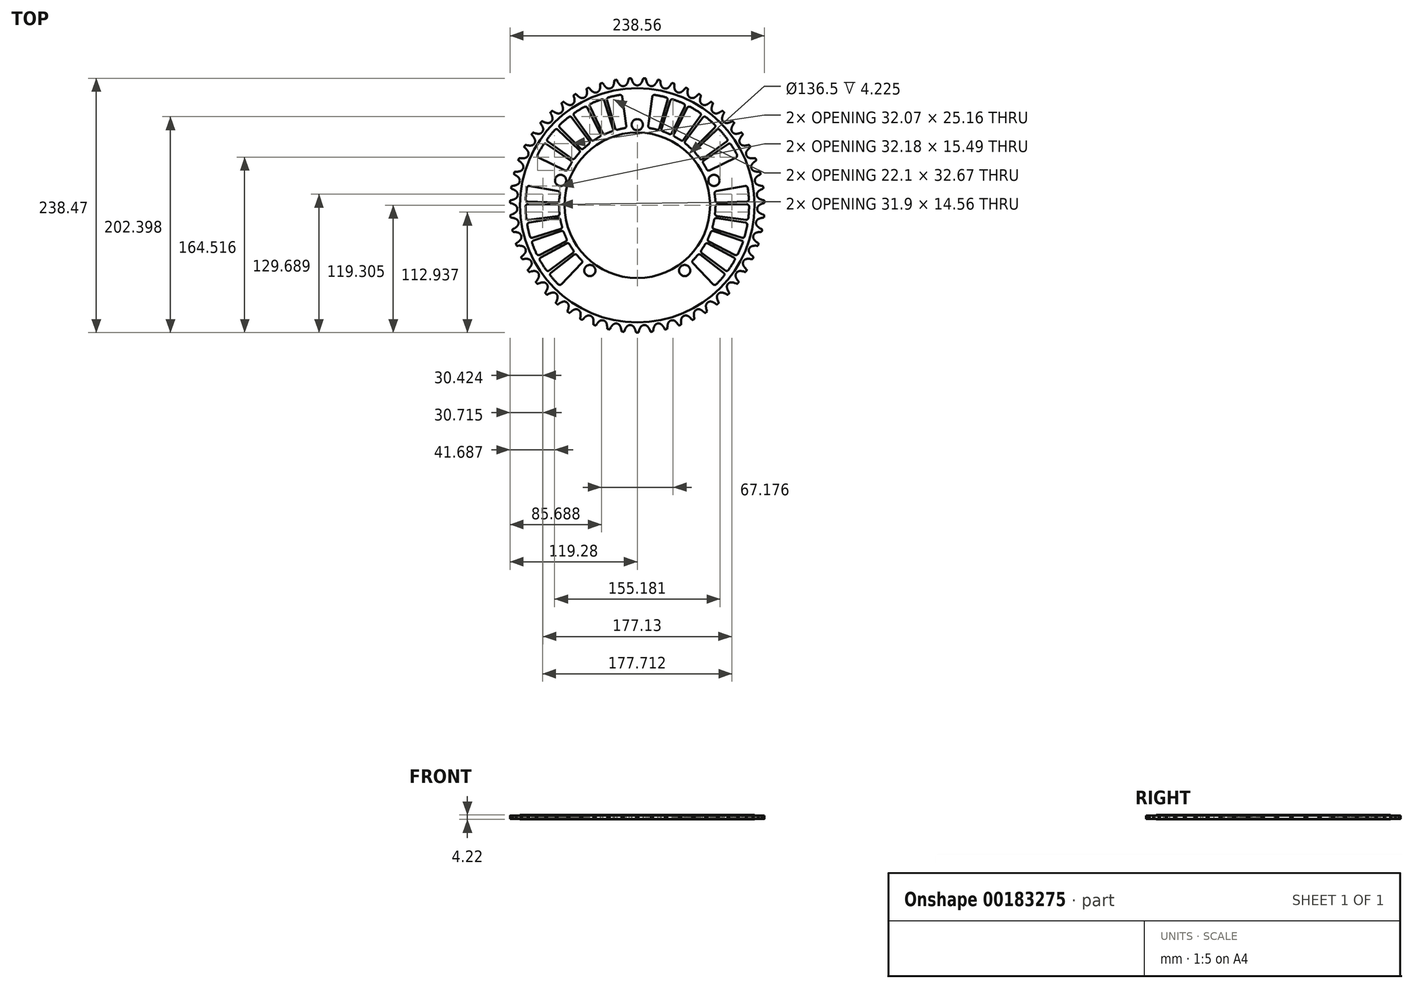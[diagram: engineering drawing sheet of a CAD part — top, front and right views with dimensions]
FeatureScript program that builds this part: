
annotation { "Feature Type Name" : "Feature", "Feature Type Description" : "" }
export const myFeature = defineFeature(function(context is Context, id is Id, definition is map)
    precondition{}
    {
        {
            var Q0;
            Q0=qCreatedBy(makeId("Top.planeOp"),FACE);
            var sketch = newSketch(context, id + "F0", { "sketchPlane" : qUnion([Q0])});
            skArc(sketch, "E0", {"start": v(-3.4, 114.25) * mm, "mid": v(-1.91, 112.97) * mm, "end": v(0, 112.52) * mm});
            skArc(sketch, "E1", {"start": v(-4.92, 117.1) * mm, "mid": v(-4.27, 115.62) * mm, "end": v(-3.4, 114.25) * mm});
            skLineSegment(sketch, "E2", {"start": v(-4.92, 117.1) * mm, "end": v(-5.32, 118.26) * mm});
            skArc(sketch, "E3", {"start": v(-5.32, 118.26) * mm, "mid": v(-5.97, 119.62) * mm, "end": v(-6.9, 120.8) * mm});
            skArc(sketch, "E4.MirrorCS", {"start": v(3.4, 114.25) * mm, "mid": v(1.91, 112.97) * mm, "end": v(0, 112.52) * mm});
            skArc(sketch, "E5.MirrorCS", {"start": v(4.92, 117.1) * mm, "mid": v(4.27, 115.62) * mm, "end": v(3.4, 114.25) * mm});
            skLineSegment(sketch, "E6.MirrorCS", {"start": v(4.92, 117.1) * mm, "end": v(5.32, 118.26) * mm});
            skArc(sketch, "E7.MirrorCS", {"start": v(5.32, 118.26) * mm, "mid": v(5.97, 119.62) * mm, "end": v(6.9, 120.8) * mm});
            skArc(sketch, "E8.1.0", {"start": v(-16.4, 113.12) * mm, "mid": v(-14.78, 112.02) * mm, "end": v(-12.83, 111.78) * mm});
            skArc(sketch, "E8.1.1", {"start": v(-8.2, 118.1) * mm, "mid": v(-7.7, 119.53) * mm, "end": v(-6.9, 120.8) * mm});
            skArc(sketch, "E8.1.2", {"start": v(-9.64, 113.9) * mm, "mid": v(-10.98, 112.46) * mm, "end": v(-12.83, 111.78) * mm});
            skArc(sketch, "E8.1.3", {"start": v(-8.46, 116.9) * mm, "mid": v(-8.94, 115.35) * mm, "end": v(-9.64, 113.9) * mm});
            skArc(sketch, "E8.1.4", {"start": v(-18.23, 115.77) * mm, "mid": v(-17.42, 114.38) * mm, "end": v(-16.4, 113.12) * mm});
            skArc(sketch, "E8.1.5", {"start": v(-18.77, 116.89) * mm, "mid": v(-19.57, 118.16) * mm, "end": v(-20.63, 119.23) * mm});
            skLineSegment(sketch, "E8.1.6", {"start": v(-18.23, 115.77) * mm, "end": v(-18.77, 116.89) * mm});
            skLineSegment(sketch, "E8.1.7", {"start": v(-8.46, 116.9) * mm, "end": v(-8.2, 118.1) * mm});
            skArc(sketch, "E8.2.0", {"start": v(-29.2, 110.5) * mm, "mid": v(-27.45, 109.6) * mm, "end": v(-25.48, 109.6) * mm});
            skArc(sketch, "E8.2.1", {"start": v(-21.6, 116.4) * mm, "mid": v(-21.28, 117.87) * mm, "end": v(-20.63, 119.23) * mm});
            skArc(sketch, "E8.2.2", {"start": v(-22.56, 112.05) * mm, "mid": v(-23.73, 110.47) * mm, "end": v(-25.48, 109.6) * mm});
            skArc(sketch, "E8.2.3", {"start": v(-21.73, 115.16) * mm, "mid": v(-22.03, 113.58) * mm, "end": v(-22.56, 112.05) * mm});
            skArc(sketch, "E8.2.4", {"start": v(-31.3, 112.94) * mm, "mid": v(-30.34, 111.65) * mm, "end": v(-29.2, 110.5) * mm});
            skArc(sketch, "E8.2.5", {"start": v(-31.97, 113.99) * mm, "mid": v(-32.9, 115.16) * mm, "end": v(-34.09, 116.1) * mm});
            skLineSegment(sketch, "E8.2.6", {"start": v(-31.3, 112.94) * mm, "end": v(-31.97, 113.99) * mm});
            skLineSegment(sketch, "E8.2.7", {"start": v(-21.73, 115.16) * mm, "end": v(-21.6, 116.4) * mm});
            skArc(sketch, "E8.3.0", {"start": v(-41.6, 106.46) * mm, "mid": v(-39.76, 105.76) * mm, "end": v(-37.8, 105.97) * mm});
            skArc(sketch, "E8.3.1", {"start": v(-34.73, 113.18) * mm, "mid": v(-34.57, 114.67) * mm, "end": v(-34.09, 116.1) * mm});
            skArc(sketch, "E8.3.2", {"start": v(-35.18, 108.75) * mm, "mid": v(-36.16, 107.05) * mm, "end": v(-37.8, 105.97) * mm});
            skArc(sketch, "E8.3.3", {"start": v(-34.72, 111.94) * mm, "mid": v(-34.83, 110.33) * mm, "end": v(-35.18, 108.75) * mm});
            skArc(sketch, "E8.3.4", {"start": v(-43.98, 108.63) * mm, "mid": v(-42.87, 107.46) * mm, "end": v(-41.6, 106.46) * mm});
            skArc(sketch, "E8.3.5", {"start": v(-44.75, 109.6) * mm, "mid": v(-45.82, 110.66) * mm, "end": v(-47.1, 111.46) * mm});
            skLineSegment(sketch, "E8.3.6", {"start": v(-43.98, 108.63) * mm, "end": v(-44.75, 109.6) * mm});
            skLineSegment(sketch, "E8.3.7", {"start": v(-34.72, 111.94) * mm, "end": v(-34.73, 113.18) * mm});
            skArc(sketch, "E8.4.0", {"start": v(-53.46, 101.02) * mm, "mid": v(-51.56, 100.54) * mm, "end": v(-49.64, 100.97) * mm});
            skArc(sketch, "E8.4.1", {"start": v(-47.4, 108.48) * mm, "mid": v(-47.42, 109.99) * mm, "end": v(-47.1, 111.46) * mm});
            skArc(sketch, "E8.4.2", {"start": v(-47.35, 104.03) * mm, "mid": v(-48.13, 102.23) * mm, "end": v(-49.64, 100.97) * mm});
            skArc(sketch, "E8.4.3", {"start": v(-47.25, 107.25) * mm, "mid": v(-47.18, 105.64) * mm, "end": v(-47.35, 104.03) * mm});
            skArc(sketch, "E8.4.4", {"start": v(-56.07, 102.91) * mm, "mid": v(-54.84, 101.87) * mm, "end": v(-53.46, 101.02) * mm});
            skArc(sketch, "E8.4.5", {"start": v(-56.95, 103.78) * mm, "mid": v(-58.14, 104.72) * mm, "end": v(-59.5, 105.36) * mm});
            skLineSegment(sketch, "E8.4.6", {"start": v(-56.07, 102.91) * mm, "end": v(-56.95, 103.78) * mm});
            skLineSegment(sketch, "E8.4.7", {"start": v(-47.25, 107.25) * mm, "end": v(-47.4, 108.48) * mm});
            skArc(sketch, "E8.5.0", {"start": v(-64.63, 94.27) * mm, "mid": v(-62.68, 94) * mm, "end": v(-60.83, 94.66) * mm});
            skArc(sketch, "E8.5.1", {"start": v(-59.46, 102.37) * mm, "mid": v(-59.65, 103.86) * mm, "end": v(-59.5, 105.36) * mm});
            skArc(sketch, "E8.5.2", {"start": v(-58.9, 97.96) * mm, "mid": v(-59.47, 96.07) * mm, "end": v(-60.83, 94.66) * mm});
            skArc(sketch, "E8.5.3", {"start": v(-59.17, 101.16) * mm, "mid": v(-58.91, 99.57) * mm, "end": v(-58.9, 97.96) * mm});
            skArc(sketch, "E8.5.4", {"start": v(-67.44, 95.85) * mm, "mid": v(-66.1, 94.96) * mm, "end": v(-64.63, 94.27) * mm});
            skArc(sketch, "E8.5.5", {"start": v(-68.41, 96.61) * mm, "mid": v(-69.7, 97.4) * mm, "end": v(-71.12, 97.9) * mm});
            skLineSegment(sketch, "E8.5.6", {"start": v(-67.44, 95.85) * mm, "end": v(-68.41, 96.61) * mm});
            skLineSegment(sketch, "E8.5.7", {"start": v(-59.17, 101.16) * mm, "end": v(-59.46, 102.37) * mm});
            skArc(sketch, "E8.6.0", {"start": v(-74.96, 86.29) * mm, "mid": v(-73, 86.25) * mm, "end": v(-71.22, 87.1) * mm});
            skArc(sketch, "E8.6.1", {"start": v(-70.74, 94.92) * mm, "mid": v(-71.1, 96.39) * mm, "end": v(-71.12, 97.9) * mm});
            skArc(sketch, "E8.6.2", {"start": v(-69.68, 90.6) * mm, "mid": v(-70.03, 88.67) * mm, "end": v(-71.22, 87.1) * mm});
            skArc(sketch, "E8.6.3", {"start": v(-70.31, 93.76) * mm, "mid": v(-69.88, 92.2) * mm, "end": v(-69.68, 90.6) * mm});
            skArc(sketch, "E8.6.4", {"start": v(-77.92, 87.54) * mm, "mid": v(-76.49, 86.8) * mm, "end": v(-74.96, 86.29) * mm});
            skArc(sketch, "E8.6.5", {"start": v(-78.98, 88.19) * mm, "mid": v(-80.34, 88.83) * mm, "end": v(-81.82, 89.15) * mm});
            skLineSegment(sketch, "E8.6.6", {"start": v(-77.92, 87.54) * mm, "end": v(-78.98, 88.19) * mm});
            skLineSegment(sketch, "E8.6.7", {"start": v(-70.31, 93.76) * mm, "end": v(-70.74, 94.92) * mm});
            skArc(sketch, "E8.7.0", {"start": v(-84.3, 77.18) * mm, "mid": v(-82.35, 77.37) * mm, "end": v(-80.69, 78.42) * mm});
            skArc(sketch, "E8.7.1", {"start": v(-81.1, 86.24) * mm, "mid": v(-81.62, 87.65) * mm, "end": v(-81.82, 89.15) * mm});
            skArc(sketch, "E8.7.2", {"start": v(-79.55, 82.07) * mm, "mid": v(-79.68, 80.1) * mm, "end": v(-80.69, 78.42) * mm});
            skArc(sketch, "E8.7.3", {"start": v(-80.54, 85.13) * mm, "mid": v(-79.94, 83.64) * mm, "end": v(-79.55, 82.07) * mm});
            skArc(sketch, "E8.7.4", {"start": v(-87.4, 78.08) * mm, "mid": v(-85.88, 77.52) * mm, "end": v(-84.3, 77.18) * mm});
            skArc(sketch, "E8.7.5", {"start": v(-88.52, 78.6) * mm, "mid": v(-89.94, 79.1) * mm, "end": v(-91.44, 79.24) * mm});
            skLineSegment(sketch, "E8.7.6", {"start": v(-87.4, 78.08) * mm, "end": v(-88.52, 78.6) * mm});
            skLineSegment(sketch, "E8.7.7", {"start": v(-80.54, 85.13) * mm, "end": v(-81.1, 86.24) * mm});
            skArc(sketch, "E8.8.0", {"start": v(-92.55, 67.07) * mm, "mid": v(-90.63, 67.48) * mm, "end": v(-89.1, 68.71) * mm});
            skArc(sketch, "E8.8.1", {"start": v(-90.4, 76.43) * mm, "mid": v(-91.08, 77.78) * mm, "end": v(-91.44, 79.24) * mm});
            skArc(sketch, "E8.8.2", {"start": v(-88.4, 72.47) * mm, "mid": v(-88.3, 70.5) * mm, "end": v(-89.1, 68.71) * mm});
            skArc(sketch, "E8.8.3", {"start": v(-89.72, 75.4) * mm, "mid": v(-88.95, 73.98) * mm, "end": v(-88.4, 72.47) * mm});
            skArc(sketch, "E8.8.4", {"start": v(-95.72, 67.61) * mm, "mid": v(-94.16, 67.22) * mm, "end": v(-92.55, 67.07) * mm});
            skArc(sketch, "E8.8.5", {"start": v(-96.9, 68) * mm, "mid": v(-98.37, 68.32) * mm, "end": v(-99.88, 68.3) * mm});
            skLineSegment(sketch, "E8.8.6", {"start": v(-95.72, 67.61) * mm, "end": v(-96.9, 68) * mm});
            skLineSegment(sketch, "E8.8.7", {"start": v(-89.72, 75.4) * mm, "end": v(-90.4, 76.43) * mm});
            skArc(sketch, "E8.9.0", {"start": v(-99.6, 56.08) * mm, "mid": v(-97.73, 56.7) * mm, "end": v(-96.35, 58.1) * mm});
            skArc(sketch, "E8.9.1", {"start": v(-98.52, 65.63) * mm, "mid": v(-99.35, 66.89) * mm, "end": v(-99.88, 68.3) * mm});
            skArc(sketch, "E8.9.2", {"start": v(-96.07, 61.92) * mm, "mid": v(-95.76, 59.98) * mm, "end": v(-96.35, 58.1) * mm});
            skArc(sketch, "E8.9.3", {"start": v(-97.73, 64.68) * mm, "mid": v(-96.8, 63.36) * mm, "end": v(-96.07, 61.92) * mm});
            skArc(sketch, "E8.9.4", {"start": v(-102.8, 56.26) * mm, "mid": v(-101.2, 56.05) * mm, "end": v(-99.6, 56.08) * mm});
            skArc(sketch, "E8.9.5", {"start": v(-104.02, 56.52) * mm, "mid": v(-105.52, 56.66) * mm, "end": v(-107.01, 56.47) * mm});
            skLineSegment(sketch, "E8.9.6", {"start": v(-102.8, 56.26) * mm, "end": v(-104.02, 56.52) * mm});
            skLineSegment(sketch, "E8.9.7", {"start": v(-97.73, 64.68) * mm, "end": v(-98.52, 65.63) * mm});
            skArc(sketch, "E8.10.0", {"start": v(-105.34, 44.36) * mm, "mid": v(-103.56, 45.2) * mm, "end": v(-102.34, 46.74) * mm});
            skArc(sketch, "E8.10.1", {"start": v(-105.36, 53.97) * mm, "mid": v(-106.33, 55.13) * mm, "end": v(-107.01, 56.47) * mm});
            skArc(sketch, "E8.10.2", {"start": v(-102.5, 50.56) * mm, "mid": v(-101.97, 48.67) * mm, "end": v(-102.34, 46.74) * mm});
            skArc(sketch, "E8.10.3", {"start": v(-104.47, 53.12) * mm, "mid": v(-103.4, 51.91) * mm, "end": v(-102.5, 50.56) * mm});
            skArc(sketch, "E8.10.4", {"start": v(-108.55, 44.17) * mm, "mid": v(-106.94, 44.15) * mm, "end": v(-105.34, 44.36) * mm});
            skArc(sketch, "E8.10.5", {"start": v(-109.78, 44.3) * mm, "mid": v(-111.3, 44.27) * mm, "end": v(-112.75, 43.9) * mm});
            skLineSegment(sketch, "E8.10.6", {"start": v(-108.55, 44.17) * mm, "end": v(-109.78, 44.3) * mm});
            skLineSegment(sketch, "E8.10.7", {"start": v(-104.47, 53.12) * mm, "end": v(-105.36, 53.97) * mm});
            skArc(sketch, "E8.11.0", {"start": v(-109.7, 32.07) * mm, "mid": v(-108.03, 33.1) * mm, "end": v(-107, 34.77) * mm});
            skArc(sketch, "E8.11.1", {"start": v(-110.83, 41.6) * mm, "mid": v(-111.92, 42.65) * mm, "end": v(-112.75, 43.9) * mm});
            skArc(sketch, "E8.11.2", {"start": v(-107.6, 38.55) * mm, "mid": v(-106.85, 36.73) * mm, "end": v(-107, 34.77) * mm});
            skArc(sketch, "E8.11.3", {"start": v(-109.84, 40.86) * mm, "mid": v(-108.63, 39.79) * mm, "end": v(-107.6, 38.55) * mm});
            skArc(sketch, "E8.11.4", {"start": v(-112.88, 31.51) * mm, "mid": v(-111.27, 31.67) * mm, "end": v(-109.7, 32.07) * mm});
            skArc(sketch, "E8.11.5", {"start": v(-114.12, 31.49) * mm, "mid": v(-115.61, 31.3) * mm, "end": v(-117.02, 30.76) * mm});
            skLineSegment(sketch, "E8.11.6", {"start": v(-112.88, 31.51) * mm, "end": v(-114.12, 31.49) * mm});
            skLineSegment(sketch, "E8.11.7", {"start": v(-109.84, 40.86) * mm, "end": v(-110.83, 41.6) * mm});
            skArc(sketch, "E8.12.0", {"start": v(-112.65, 19.35) * mm, "mid": v(-111.1, 20.57) * mm, "end": v(-110.27, 22.35) * mm});
            skArc(sketch, "E8.12.1", {"start": v(-114.85, 28.7) * mm, "mid": v(-116.05, 29.61) * mm, "end": v(-117.02, 30.76) * mm});
            skArc(sketch, "E8.12.2", {"start": v(-111.3, 26.03) * mm, "mid": v(-110.34, 24.31) * mm, "end": v(-110.27, 22.35) * mm});
            skArc(sketch, "E8.12.3", {"start": v(-113.78, 28.07) * mm, "mid": v(-112.46, 27.15) * mm, "end": v(-111.3, 26.03) * mm});
            skArc(sketch, "E8.12.4", {"start": v(-115.73, 18.44) * mm, "mid": v(-114.16, 18.78) * mm, "end": v(-112.65, 19.35) * mm});
            skArc(sketch, "E8.12.5", {"start": v(-116.96, 18.28) * mm, "mid": v(-118.42, 17.9) * mm, "end": v(-119.77, 17.22) * mm});
            skLineSegment(sketch, "E8.12.6", {"start": v(-115.73, 18.44) * mm, "end": v(-116.96, 18.28) * mm});
            skLineSegment(sketch, "E8.12.7", {"start": v(-113.78, 28.07) * mm, "end": v(-114.85, 28.7) * mm});
            skArc(sketch, "E8.13.0", {"start": v(-114.12, 6.39) * mm, "mid": v(-112.72, 7.77) * mm, "end": v(-112.1, 9.63) * mm});
            skArc(sketch, "E8.13.1", {"start": v(-117.37, 15.43) * mm, "mid": v(-118.67, 16.19) * mm, "end": v(-119.77, 17.22) * mm});
            skArc(sketch, "E8.13.2", {"start": v(-113.53, 13.18) * mm, "mid": v(-112.4, 11.58) * mm, "end": v(-112.1, 9.63) * mm});
            skArc(sketch, "E8.13.3", {"start": v(-116.24, 14.92) * mm, "mid": v(-114.82, 14.15) * mm, "end": v(-113.53, 13.18) * mm});
            skArc(sketch, "E8.13.4", {"start": v(-117.08, 5.13) * mm, "mid": v(-115.55, 5.65) * mm, "end": v(-114.12, 6.39) * mm});
            skArc(sketch, "E8.13.5", {"start": v(-118.28, 4.82) * mm, "mid": v(-119.7, 4.3) * mm, "end": v(-120.95, 3.46) * mm});
            skLineSegment(sketch, "E8.13.6", {"start": v(-117.08, 5.13) * mm, "end": v(-118.28, 4.82) * mm});
            skLineSegment(sketch, "E8.13.7", {"start": v(-116.24, 14.92) * mm, "end": v(-117.37, 15.43) * mm});
            skArc(sketch, "E8.14.0", {"start": v(-114.1, -6.66) * mm, "mid": v(-112.87, -5.13) * mm, "end": v(-112.47, -3.2) * mm});
            skArc(sketch, "E8.14.1", {"start": v(-118.36, 1.95) * mm, "mid": v(-119.74, 2.56) * mm, "end": v(-120.95, 3.46) * mm});
            skArc(sketch, "E8.14.2", {"start": v(-114.3, 0.15) * mm, "mid": v(-112.98, -1.31) * mm, "end": v(-112.47, -3.2) * mm});
            skArc(sketch, "E8.14.3", {"start": v(-117.18, 1.57) * mm, "mid": v(-115.69, 0.97) * mm, "end": v(-114.3, 0.15) * mm});
            skArc(sketch, "E8.14.4", {"start": v(-116.9, -8.25) * mm, "mid": v(-115.44, -7.56) * mm, "end": v(-114.1, -6.66) * mm});
            skArc(sketch, "E8.14.5", {"start": v(-118.06, -8.7) * mm, "mid": v(-119.4, -9.38) * mm, "end": v(-120.55, -10.35) * mm});
            skLineSegment(sketch, "E8.14.6", {"start": v(-116.9, -8.25) * mm, "end": v(-118.06, -8.7) * mm});
            skLineSegment(sketch, "E8.14.7", {"start": v(-117.18, 1.57) * mm, "end": v(-118.36, 1.95) * mm});
            skArc(sketch, "E8.15.0", {"start": v(-112.6, -19.63) * mm, "mid": v(-111.55, -17.96) * mm, "end": v(-111.37, -16) * mm});
            skArc(sketch, "E8.15.1", {"start": v(-117.81, -11.56) * mm, "mid": v(-119.25, -11.1) * mm, "end": v(-120.55, -10.35) * mm});
            skArc(sketch, "E8.15.2", {"start": v(-113.57, -12.88) * mm, "mid": v(-112.1, -14.18) * mm, "end": v(-111.37, -16) * mm});
            skArc(sketch, "E8.15.3", {"start": v(-116.6, -11.8) * mm, "mid": v(-115.04, -12.23) * mm, "end": v(-113.57, -12.88) * mm});
            skArc(sketch, "E8.15.4", {"start": v(-115.2, -21.52) * mm, "mid": v(-113.83, -20.67) * mm, "end": v(-112.6, -19.63) * mm});
            skArc(sketch, "E8.15.5", {"start": v(-116.3, -22.1) * mm, "mid": v(-117.55, -22.93) * mm, "end": v(-118.59, -24.02) * mm});
            skLineSegment(sketch, "E8.15.6", {"start": v(-115.2, -21.52) * mm, "end": v(-116.3, -22.1) * mm});
            skLineSegment(sketch, "E8.15.7", {"start": v(-116.6, -11.8) * mm, "end": v(-117.81, -11.56) * mm});
            skArc(sketch, "E8.16.0", {"start": v(-109.63, -32.33) * mm, "mid": v(-108.77, -30.56) * mm, "end": v(-108.82, -28.6) * mm});
            skArc(sketch, "E8.16.1", {"start": v(-115.73, -24.91) * mm, "mid": v(-117.2, -24.63) * mm, "end": v(-118.59, -24.02) * mm});
            skArc(sketch, "E8.16.2", {"start": v(-111.36, -25.74) * mm, "mid": v(-109.74, -26.87) * mm, "end": v(-108.82, -28.6) * mm});
            skArc(sketch, "E8.16.3", {"start": v(-114.5, -25) * mm, "mid": v(-112.9, -25.26) * mm, "end": v(-111.36, -25.74) * mm});
            skArc(sketch, "E8.16.4", {"start": v(-112, -34.52) * mm, "mid": v(-110.73, -33.51) * mm, "end": v(-109.63, -32.33) * mm});
            skArc(sketch, "E8.16.5", {"start": v(-113.02, -35.2) * mm, "mid": v(-114.17, -36.18) * mm, "end": v(-115.08, -37.39) * mm});
            skLineSegment(sketch, "E8.16.6", {"start": v(-112, -34.52) * mm, "end": v(-113.02, -35.2) * mm});
            skLineSegment(sketch, "E8.16.7", {"start": v(-114.5, -25) * mm, "end": v(-115.73, -24.91) * mm});
            skArc(sketch, "E8.17.0", {"start": v(-105.22, -44.62) * mm, "mid": v(-104.58, -42.76) * mm, "end": v(-104.85, -40.82) * mm});
            skArc(sketch, "E8.17.1", {"start": v(-112.13, -37.94) * mm, "mid": v(-113.64, -37.83) * mm, "end": v(-115.08, -37.39) * mm});
            skArc(sketch, "E8.17.2", {"start": v(-107.7, -38.27) * mm, "mid": v(-105.97, -39.2) * mm, "end": v(-104.85, -40.82) * mm});
            skArc(sketch, "E8.17.3", {"start": v(-110.9, -37.9) * mm, "mid": v(-109.28, -37.96) * mm, "end": v(-107.7, -38.27) * mm});
            skArc(sketch, "E8.17.4", {"start": v(-107.33, -47.06) * mm, "mid": v(-106.19, -45.92) * mm, "end": v(-105.22, -44.62) * mm});
            skArc(sketch, "E8.17.5", {"start": v(-108.27, -47.86) * mm, "mid": v(-109.3, -48.96) * mm, "end": v(-110.06, -50.26) * mm});
            skLineSegment(sketch, "E8.17.6", {"start": v(-107.33, -47.06) * mm, "end": v(-108.27, -47.86) * mm});
            skLineSegment(sketch, "E8.17.7", {"start": v(-110.9, -37.9) * mm, "end": v(-112.13, -37.94) * mm});
            skArc(sketch, "E8.18.0", {"start": v(-99.45, -56.32) * mm, "mid": v(-99.02, -54.4) * mm, "end": v(-99.5, -52.5) * mm});
            skArc(sketch, "E8.18.1", {"start": v(-107.08, -50.48) * mm, "mid": v(-108.58, -50.54) * mm, "end": v(-110.06, -50.26) * mm});
            skArc(sketch, "E8.18.2", {"start": v(-102.63, -50.3) * mm, "mid": v(-100.8, -51.02) * mm, "end": v(-99.5, -52.5) * mm});
            skArc(sketch, "E8.18.3", {"start": v(-105.85, -50.3) * mm, "mid": v(-104.24, -50.17) * mm, "end": v(-102.63, -50.3) * mm});
            skArc(sketch, "E8.18.4", {"start": v(-101.26, -58.98) * mm, "mid": v(-100.26, -57.72) * mm, "end": v(-99.45, -56.32) * mm});
            skArc(sketch, "E8.18.5", {"start": v(-102.11, -59.89) * mm, "mid": v(-103, -61.1) * mm, "end": v(-103.62, -62.48) * mm});
            skLineSegment(sketch, "E8.18.6", {"start": v(-101.26, -58.98) * mm, "end": v(-102.11, -59.89) * mm});
            skLineSegment(sketch, "E8.18.7", {"start": v(-105.85, -50.3) * mm, "end": v(-107.08, -50.48) * mm});
            skArc(sketch, "E8.19.0", {"start": v(-92.38, -67.3) * mm, "mid": v(-92.18, -65.34) * mm, "end": v(-92.88, -63.5) * mm});
            skArc(sketch, "E8.19.1", {"start": v(-100.62, -62.35) * mm, "mid": v(-102.11, -62.59) * mm, "end": v(-103.62, -62.48) * mm});
            skArc(sketch, "E8.19.2", {"start": v(-96.23, -61.67) * mm, "mid": v(-94.33, -62.18) * mm, "end": v(-92.88, -63.5) * mm});
            skArc(sketch, "E8.19.3", {"start": v(-99.43, -62.03) * mm, "mid": v(-97.84, -61.73) * mm, "end": v(-96.23, -61.67) * mm});
            skArc(sketch, "E8.19.4", {"start": v(-93.88, -70.14) * mm, "mid": v(-93.03, -68.77) * mm, "end": v(-92.38, -67.3) * mm});
            skArc(sketch, "E8.19.5", {"start": v(-94.62, -71.14) * mm, "mid": v(-95.37, -72.44) * mm, "end": v(-95.82, -73.88) * mm});
            skLineSegment(sketch, "E8.19.6", {"start": v(-93.88, -70.14) * mm, "end": v(-94.62, -71.14) * mm});
            skLineSegment(sketch, "E8.19.7", {"start": v(-99.43, -62.03) * mm, "end": v(-100.62, -62.35) * mm});
            skArc(sketch, "E8.20.0", {"start": v(-84.1, -77.38) * mm, "mid": v(-84.13, -75.42) * mm, "end": v(-85.03, -73.68) * mm});
            skArc(sketch, "E8.20.1", {"start": v(-92.86, -73.42) * mm, "mid": v(-94.31, -73.82) * mm, "end": v(-95.82, -73.88) * mm});
            skArc(sketch, "E8.20.2", {"start": v(-88.57, -72.23) * mm, "mid": v(-86.63, -72.53) * mm, "end": v(-85.03, -73.68) * mm});
            skArc(sketch, "E8.20.3", {"start": v(-91.7, -72.96) * mm, "mid": v(-90.17, -72.48) * mm, "end": v(-88.57, -72.23) * mm});
            skArc(sketch, "E8.20.4", {"start": v(-85.27, -80.39) * mm, "mid": v(-84.58, -78.93) * mm, "end": v(-84.1, -77.38) * mm});
            skArc(sketch, "E8.20.5", {"start": v(-85.9, -81.46) * mm, "mid": v(-86.5, -82.84) * mm, "end": v(-86.77, -84.32) * mm});
            skLineSegment(sketch, "E8.20.6", {"start": v(-85.27, -80.39) * mm, "end": v(-85.9, -81.46) * mm});
            skLineSegment(sketch, "E8.20.7", {"start": v(-91.7, -72.96) * mm, "end": v(-92.86, -73.42) * mm});
            skArc(sketch, "E8.21.0", {"start": v(-74.74, -86.47) * mm, "mid": v(-74.98, -84.52) * mm, "end": v(-76.08, -82.89) * mm});
            skArc(sketch, "E8.21.1", {"start": v(-83.88, -83.52) * mm, "mid": v(-85.28, -84.09) * mm, "end": v(-86.77, -84.32) * mm});
            skArc(sketch, "E8.21.2", {"start": v(-79.76, -81.86) * mm, "mid": v(-77.8, -81.93) * mm, "end": v(-76.08, -82.89) * mm});
            skArc(sketch, "E8.21.3", {"start": v(-82.8, -82.94) * mm, "mid": v(-81.32, -82.29) * mm, "end": v(-79.76, -81.86) * mm});
            skArc(sketch, "E8.21.4", {"start": v(-75.55, -89.58) * mm, "mid": v(-75.03, -88.06) * mm, "end": v(-74.74, -86.47) * mm});
            skArc(sketch, "E8.21.5", {"start": v(-76.04, -90.72) * mm, "mid": v(-76.49, -92.16) * mm, "end": v(-76.6, -93.66) * mm});
            skLineSegment(sketch, "E8.21.6", {"start": v(-75.55, -89.58) * mm, "end": v(-76.04, -90.72) * mm});
            skLineSegment(sketch, "E8.21.7", {"start": v(-82.8, -82.94) * mm, "end": v(-83.88, -83.52) * mm});
            skArc(sketch, "E8.22.0", {"start": v(-64.4, -94.42) * mm, "mid": v(-64.86, -92.51) * mm, "end": v(-66.13, -91.02) * mm});
            skArc(sketch, "E8.22.1", {"start": v(-73.82, -92.54) * mm, "mid": v(-75.14, -93.26) * mm, "end": v(-76.6, -93.66) * mm});
            skArc(sketch, "E8.22.2", {"start": v(-69.9, -90.42) * mm, "mid": v(-67.95, -90.27) * mm, "end": v(-66.13, -91.02) * mm});
            skArc(sketch, "E8.22.3", {"start": v(-72.8, -91.83) * mm, "mid": v(-71.4, -91.02) * mm, "end": v(-69.9, -90.42) * mm});
            skArc(sketch, "E8.22.4", {"start": v(-64.85, -97.61) * mm, "mid": v(-64.5, -96.03) * mm, "end": v(-64.4, -94.42) * mm});
            skArc(sketch, "E8.22.5", {"start": v(-65.2, -98.8) * mm, "mid": v(-65.48, -100.28) * mm, "end": v(-65.42, -101.79) * mm});
            skLineSegment(sketch, "E8.22.6", {"start": v(-64.85, -97.61) * mm, "end": v(-65.2, -98.8) * mm});
            skLineSegment(sketch, "E8.22.7", {"start": v(-72.8, -91.83) * mm, "end": v(-73.82, -92.54) * mm});
            skArc(sketch, "E8.23.0", {"start": v(-53.21, -101.15) * mm, "mid": v(-53.89, -99.3) * mm, "end": v(-55.33, -97.96) * mm});
            skArc(sketch, "E8.23.1", {"start": v(-62.79, -100.35) * mm, "mid": v(-64.02, -101.22) * mm, "end": v(-65.42, -101.79) * mm});
            skArc(sketch, "E8.23.2", {"start": v(-59.14, -97.8) * mm, "mid": v(-57.22, -97.42) * mm, "end": v(-55.33, -97.96) * mm});
            skArc(sketch, "E8.23.3", {"start": v(-61.86, -99.53) * mm, "mid": v(-60.56, -98.57) * mm, "end": v(-59.14, -97.8) * mm});
            skArc(sketch, "E8.23.4", {"start": v(-53.3, -104.37) * mm, "mid": v(-53.13, -102.76) * mm, "end": v(-53.21, -101.15) * mm});
            skArc(sketch, "E8.23.5", {"start": v(-53.52, -105.59) * mm, "mid": v(-53.62, -107.09) * mm, "end": v(-53.39, -108.58) * mm});
            skLineSegment(sketch, "E8.23.6", {"start": v(-53.3, -104.37) * mm, "end": v(-53.52, -105.59) * mm});
            skLineSegment(sketch, "E8.23.7", {"start": v(-61.86, -99.53) * mm, "end": v(-62.79, -100.35) * mm});
            skArc(sketch, "E8.24.0", {"start": v(-41.33, -106.56) * mm, "mid": v(-42.22, -104.8) * mm, "end": v(-43.8, -103.63) * mm});
            skArc(sketch, "E8.24.1", {"start": v(-50.94, -106.86) * mm, "mid": v(-52.06, -107.86) * mm, "end": v(-53.39, -108.58) * mm});
            skArc(sketch, "E8.24.2", {"start": v(-47.61, -103.9) * mm, "mid": v(-45.74, -103.31) * mm, "end": v(-43.8, -103.63) * mm});
            skArc(sketch, "E8.24.3", {"start": v(-50.1, -105.94) * mm, "mid": v(-48.93, -104.83) * mm, "end": v(-47.61, -103.9) * mm});
            skArc(sketch, "E8.24.4", {"start": v(-41.05, -109.76) * mm, "mid": v(-41.07, -108.15) * mm, "end": v(-41.33, -106.56) * mm});
            skArc(sketch, "E8.24.5", {"start": v(-41.13, -111) * mm, "mid": v(-41.06, -112.5) * mm, "end": v(-40.66, -113.96) * mm});
            skLineSegment(sketch, "E8.24.6", {"start": v(-41.05, -109.76) * mm, "end": v(-41.13, -111) * mm});
            skLineSegment(sketch, "E8.24.7", {"start": v(-50.1, -105.94) * mm, "end": v(-50.94, -106.86) * mm});
            skArc(sketch, "E8.25.0", {"start": v(-28.92, -110.57) * mm, "mid": v(-30, -108.93) * mm, "end": v(-31.7, -107.95) * mm});
            skArc(sketch, "E8.25.1", {"start": v(-38.42, -111.97) * mm, "mid": v(-39.43, -113.09) * mm, "end": v(-40.66, -113.96) * mm});
            skArc(sketch, "E8.25.2", {"start": v(-35.46, -108.65) * mm, "mid": v(-33.66, -107.85) * mm, "end": v(-31.7, -107.95) * mm});
            skArc(sketch, "E8.25.3", {"start": v(-37.7, -110.96) * mm, "mid": v(-36.67, -109.72) * mm, "end": v(-35.46, -108.65) * mm});
            skArc(sketch, "E8.25.4", {"start": v(-28.27, -113.73) * mm, "mid": v(-28.48, -112.13) * mm, "end": v(-28.92, -110.57) * mm});
            skArc(sketch, "E8.25.5", {"start": v(-28.21, -114.96) * mm, "mid": v(-27.97, -116.45) * mm, "end": v(-27.4, -117.85) * mm});
            skLineSegment(sketch, "E8.25.6", {"start": v(-28.27, -113.73) * mm, "end": v(-28.21, -114.96) * mm});
            skLineSegment(sketch, "E8.25.7", {"start": v(-37.7, -110.96) * mm, "end": v(-38.42, -111.97) * mm});
            skArc(sketch, "E8.26.0", {"start": v(-16.12, -113.15) * mm, "mid": v(-17.38, -111.64) * mm, "end": v(-19.19, -110.86) * mm});
            skArc(sketch, "E8.26.1", {"start": v(-25.4, -115.62) * mm, "mid": v(-26.28, -116.85) * mm, "end": v(-27.4, -117.85) * mm});
            skArc(sketch, "E8.26.2", {"start": v(-22.84, -111.99) * mm, "mid": v(-21.15, -110.99) * mm, "end": v(-19.19, -110.86) * mm});
            skArc(sketch, "E8.26.3", {"start": v(-24.8, -114.53) * mm, "mid": v(-23.92, -113.19) * mm, "end": v(-22.84, -111.99) * mm});
            skArc(sketch, "E8.26.4", {"start": v(-15.12, -116.2) * mm, "mid": v(-15.51, -114.64) * mm, "end": v(-16.12, -113.15) * mm});
            skArc(sketch, "E8.26.5", {"start": v(-14.92, -117.43) * mm, "mid": v(-14.51, -118.88) * mm, "end": v(-13.8, -120.2) * mm});
            skLineSegment(sketch, "E8.26.6", {"start": v(-15.12, -116.2) * mm, "end": v(-14.92, -117.43) * mm});
            skLineSegment(sketch, "E8.26.7", {"start": v(-24.8, -114.53) * mm, "end": v(-25.4, -115.62) * mm});
            skArc(sketch, "E8.27.0", {"start": v(-3.12, -114.25) * mm, "mid": v(-4.54, -112.9) * mm, "end": v(-6.42, -112.32) * mm});
            skArc(sketch, "E8.27.1", {"start": v(-12.06, -117.76) * mm, "mid": v(-12.79, -119.08) * mm, "end": v(-13.8, -120.2) * mm});
            skArc(sketch, "E8.27.2", {"start": v(-9.92, -113.86) * mm, "mid": v(-8.36, -112.67) * mm, "end": v(-6.42, -112.32) * mm});
            skArc(sketch, "E8.27.3", {"start": v(-11.6, -116.61) * mm, "mid": v(-10.86, -115.17) * mm, "end": v(-9.92, -113.86) * mm});
            skArc(sketch, "E8.27.4", {"start": v(-1.78, -117.17) * mm, "mid": v(-2.34, -115.66) * mm, "end": v(-3.12, -114.25) * mm});
            skArc(sketch, "E8.27.5", {"start": v(-1.44, -118.37) * mm, "mid": v(-0.87, -119.76) * mm, "end": v(0, -121) * mm});
            skLineSegment(sketch, "E8.27.6", {"start": v(-1.78, -117.17) * mm, "end": v(-1.44, -118.37) * mm});
            skLineSegment(sketch, "E8.27.7", {"start": v(-11.6, -116.61) * mm, "end": v(-12.06, -117.76) * mm});
            skArc(sketch, "E8.28.0", {"start": v(9.92, -113.86) * mm, "mid": v(8.36, -112.67) * mm, "end": v(6.42, -112.32) * mm});
            skArc(sketch, "E8.28.1", {"start": v(1.44, -118.37) * mm, "mid": v(0.87, -119.76) * mm, "end": v(0, -121) * mm});
            skArc(sketch, "E8.28.2", {"start": v(3.12, -114.25) * mm, "mid": v(4.54, -112.9) * mm, "end": v(6.42, -112.32) * mm});
            skArc(sketch, "E8.28.3", {"start": v(1.78, -117.17) * mm, "mid": v(2.34, -115.66) * mm, "end": v(3.12, -114.25) * mm});
            skArc(sketch, "E8.28.4", {"start": v(11.6, -116.61) * mm, "mid": v(10.86, -115.17) * mm, "end": v(9.92, -113.86) * mm});
            skArc(sketch, "E8.28.5", {"start": v(12.06, -117.76) * mm, "mid": v(12.79, -119.08) * mm, "end": v(13.8, -120.2) * mm});
            skLineSegment(sketch, "E8.28.6", {"start": v(11.6, -116.61) * mm, "end": v(12.06, -117.76) * mm});
            skLineSegment(sketch, "E8.28.7", {"start": v(1.78, -117.17) * mm, "end": v(1.44, -118.37) * mm});
            skArc(sketch, "E8.29.0", {"start": v(22.84, -111.99) * mm, "mid": v(21.15, -110.99) * mm, "end": v(19.19, -110.86) * mm});
            skArc(sketch, "E8.29.1", {"start": v(14.92, -117.43) * mm, "mid": v(14.51, -118.88) * mm, "end": v(13.8, -120.2) * mm});
            skArc(sketch, "E8.29.2", {"start": v(16.12, -113.15) * mm, "mid": v(17.38, -111.64) * mm, "end": v(19.19, -110.86) * mm});
            skArc(sketch, "E8.29.3", {"start": v(15.12, -116.2) * mm, "mid": v(15.51, -114.64) * mm, "end": v(16.12, -113.15) * mm});
            skArc(sketch, "E8.29.4", {"start": v(24.8, -114.53) * mm, "mid": v(23.92, -113.19) * mm, "end": v(22.84, -111.99) * mm});
            skArc(sketch, "E8.29.5", {"start": v(25.4, -115.62) * mm, "mid": v(26.28, -116.85) * mm, "end": v(27.4, -117.85) * mm});
            skLineSegment(sketch, "E8.29.6", {"start": v(24.8, -114.53) * mm, "end": v(25.4, -115.62) * mm});
            skLineSegment(sketch, "E8.29.7", {"start": v(15.12, -116.2) * mm, "end": v(14.92, -117.43) * mm});
            skArc(sketch, "E8.30.0", {"start": v(35.46, -108.65) * mm, "mid": v(33.66, -107.85) * mm, "end": v(31.7, -107.95) * mm});
            skArc(sketch, "E8.30.1", {"start": v(28.21, -114.96) * mm, "mid": v(27.97, -116.45) * mm, "end": v(27.4, -117.85) * mm});
            skArc(sketch, "E8.30.2", {"start": v(28.92, -110.57) * mm, "mid": v(30, -108.93) * mm, "end": v(31.7, -107.95) * mm});
            skArc(sketch, "E8.30.3", {"start": v(28.27, -113.73) * mm, "mid": v(28.48, -112.13) * mm, "end": v(28.92, -110.57) * mm});
            skArc(sketch, "E8.30.4", {"start": v(37.7, -110.96) * mm, "mid": v(36.67, -109.72) * mm, "end": v(35.46, -108.65) * mm});
            skArc(sketch, "E8.30.5", {"start": v(38.42, -111.97) * mm, "mid": v(39.43, -113.09) * mm, "end": v(40.66, -113.96) * mm});
            skLineSegment(sketch, "E8.30.6", {"start": v(37.7, -110.96) * mm, "end": v(38.42, -111.97) * mm});
            skLineSegment(sketch, "E8.30.7", {"start": v(28.27, -113.73) * mm, "end": v(28.21, -114.96) * mm});
            skArc(sketch, "E8.31.0", {"start": v(47.61, -103.9) * mm, "mid": v(45.74, -103.31) * mm, "end": v(43.8, -103.63) * mm});
            skArc(sketch, "E8.31.1", {"start": v(41.13, -111) * mm, "mid": v(41.06, -112.5) * mm, "end": v(40.66, -113.96) * mm});
            skArc(sketch, "E8.31.2", {"start": v(41.33, -106.56) * mm, "mid": v(42.22, -104.8) * mm, "end": v(43.8, -103.63) * mm});
            skArc(sketch, "E8.31.3", {"start": v(41.05, -109.76) * mm, "mid": v(41.07, -108.15) * mm, "end": v(41.33, -106.56) * mm});
            skArc(sketch, "E8.31.4", {"start": v(50.1, -105.94) * mm, "mid": v(48.93, -104.83) * mm, "end": v(47.61, -103.9) * mm});
            skArc(sketch, "E8.31.5", {"start": v(50.94, -106.86) * mm, "mid": v(52.06, -107.86) * mm, "end": v(53.39, -108.58) * mm});
            skLineSegment(sketch, "E8.31.6", {"start": v(50.1, -105.94) * mm, "end": v(50.94, -106.86) * mm});
            skLineSegment(sketch, "E8.31.7", {"start": v(41.05, -109.76) * mm, "end": v(41.13, -111) * mm});
            skArc(sketch, "E8.32.0", {"start": v(59.14, -97.8) * mm, "mid": v(57.22, -97.42) * mm, "end": v(55.33, -97.96) * mm});
            skArc(sketch, "E8.32.1", {"start": v(53.52, -105.59) * mm, "mid": v(53.62, -107.09) * mm, "end": v(53.39, -108.58) * mm});
            skArc(sketch, "E8.32.2", {"start": v(53.21, -101.15) * mm, "mid": v(53.89, -99.3) * mm, "end": v(55.33, -97.96) * mm});
            skArc(sketch, "E8.32.3", {"start": v(53.3, -104.37) * mm, "mid": v(53.13, -102.76) * mm, "end": v(53.21, -101.15) * mm});
            skArc(sketch, "E8.32.4", {"start": v(61.86, -99.53) * mm, "mid": v(60.56, -98.57) * mm, "end": v(59.14, -97.8) * mm});
            skArc(sketch, "E8.32.5", {"start": v(62.79, -100.35) * mm, "mid": v(64.02, -101.22) * mm, "end": v(65.42, -101.79) * mm});
            skLineSegment(sketch, "E8.32.6", {"start": v(61.86, -99.53) * mm, "end": v(62.79, -100.35) * mm});
            skLineSegment(sketch, "E8.32.7", {"start": v(53.3, -104.37) * mm, "end": v(53.52, -105.59) * mm});
            skArc(sketch, "E8.33.0", {"start": v(69.9, -90.42) * mm, "mid": v(67.95, -90.27) * mm, "end": v(66.13, -91.02) * mm});
            skArc(sketch, "E8.33.1", {"start": v(65.2, -98.8) * mm, "mid": v(65.48, -100.28) * mm, "end": v(65.42, -101.79) * mm});
            skArc(sketch, "E8.33.2", {"start": v(64.4, -94.42) * mm, "mid": v(64.86, -92.51) * mm, "end": v(66.13, -91.02) * mm});
            skArc(sketch, "E8.33.3", {"start": v(64.85, -97.61) * mm, "mid": v(64.5, -96.03) * mm, "end": v(64.4, -94.42) * mm});
            skArc(sketch, "E8.33.4", {"start": v(72.8, -91.83) * mm, "mid": v(71.4, -91.02) * mm, "end": v(69.9, -90.42) * mm});
            skArc(sketch, "E8.33.5", {"start": v(73.82, -92.54) * mm, "mid": v(75.14, -93.26) * mm, "end": v(76.6, -93.66) * mm});
            skLineSegment(sketch, "E8.33.6", {"start": v(72.8, -91.83) * mm, "end": v(73.82, -92.54) * mm});
            skLineSegment(sketch, "E8.33.7", {"start": v(64.85, -97.61) * mm, "end": v(65.2, -98.8) * mm});
            skArc(sketch, "E8.34.0", {"start": v(79.76, -81.86) * mm, "mid": v(77.8, -81.93) * mm, "end": v(76.08, -82.89) * mm});
            skArc(sketch, "E8.34.1", {"start": v(76.04, -90.72) * mm, "mid": v(76.49, -92.16) * mm, "end": v(76.6, -93.66) * mm});
            skArc(sketch, "E8.34.2", {"start": v(74.74, -86.47) * mm, "mid": v(74.98, -84.52) * mm, "end": v(76.08, -82.89) * mm});
            skArc(sketch, "E8.34.3", {"start": v(75.55, -89.58) * mm, "mid": v(75.03, -88.06) * mm, "end": v(74.74, -86.47) * mm});
            skArc(sketch, "E8.34.4", {"start": v(82.8, -82.94) * mm, "mid": v(81.32, -82.29) * mm, "end": v(79.76, -81.86) * mm});
            skArc(sketch, "E8.34.5", {"start": v(83.88, -83.52) * mm, "mid": v(85.28, -84.09) * mm, "end": v(86.77, -84.32) * mm});
            skLineSegment(sketch, "E8.34.6", {"start": v(82.8, -82.94) * mm, "end": v(83.88, -83.52) * mm});
            skLineSegment(sketch, "E8.34.7", {"start": v(75.55, -89.58) * mm, "end": v(76.04, -90.72) * mm});
            skArc(sketch, "E8.35.0", {"start": v(88.57, -72.23) * mm, "mid": v(86.63, -72.53) * mm, "end": v(85.03, -73.68) * mm});
            skArc(sketch, "E8.35.1", {"start": v(85.9, -81.46) * mm, "mid": v(86.5, -82.84) * mm, "end": v(86.77, -84.32) * mm});
            skArc(sketch, "E8.35.2", {"start": v(84.1, -77.38) * mm, "mid": v(84.13, -75.42) * mm, "end": v(85.03, -73.68) * mm});
            skArc(sketch, "E8.35.3", {"start": v(85.27, -80.39) * mm, "mid": v(84.58, -78.93) * mm, "end": v(84.1, -77.38) * mm});
            skArc(sketch, "E8.35.4", {"start": v(91.7, -72.96) * mm, "mid": v(90.17, -72.48) * mm, "end": v(88.57, -72.23) * mm});
            skArc(sketch, "E8.35.5", {"start": v(92.86, -73.42) * mm, "mid": v(94.31, -73.82) * mm, "end": v(95.82, -73.88) * mm});
            skLineSegment(sketch, "E8.35.6", {"start": v(91.7, -72.96) * mm, "end": v(92.86, -73.42) * mm});
            skLineSegment(sketch, "E8.35.7", {"start": v(85.27, -80.39) * mm, "end": v(85.9, -81.46) * mm});
            skArc(sketch, "E8.36.0", {"start": v(96.23, -61.67) * mm, "mid": v(94.33, -62.18) * mm, "end": v(92.88, -63.5) * mm});
            skArc(sketch, "E8.36.1", {"start": v(94.62, -71.14) * mm, "mid": v(95.37, -72.44) * mm, "end": v(95.82, -73.88) * mm});
            skArc(sketch, "E8.36.2", {"start": v(92.38, -67.3) * mm, "mid": v(92.18, -65.34) * mm, "end": v(92.88, -63.5) * mm});
            skArc(sketch, "E8.36.3", {"start": v(93.88, -70.14) * mm, "mid": v(93.03, -68.77) * mm, "end": v(92.38, -67.3) * mm});
            skArc(sketch, "E8.36.4", {"start": v(99.43, -62.03) * mm, "mid": v(97.84, -61.73) * mm, "end": v(96.23, -61.67) * mm});
            skArc(sketch, "E8.36.5", {"start": v(100.62, -62.35) * mm, "mid": v(102.11, -62.59) * mm, "end": v(103.62, -62.48) * mm});
            skLineSegment(sketch, "E8.36.6", {"start": v(99.43, -62.03) * mm, "end": v(100.62, -62.35) * mm});
            skLineSegment(sketch, "E8.36.7", {"start": v(93.88, -70.14) * mm, "end": v(94.62, -71.14) * mm});
            skArc(sketch, "E8.37.0", {"start": v(102.63, -50.3) * mm, "mid": v(100.8, -51.02) * mm, "end": v(99.5, -52.5) * mm});
            skArc(sketch, "E8.37.1", {"start": v(102.11, -59.89) * mm, "mid": v(103, -61.1) * mm, "end": v(103.62, -62.48) * mm});
            skArc(sketch, "E8.37.2", {"start": v(99.45, -56.32) * mm, "mid": v(99.02, -54.4) * mm, "end": v(99.5, -52.5) * mm});
            skArc(sketch, "E8.37.3", {"start": v(101.26, -58.98) * mm, "mid": v(100.26, -57.72) * mm, "end": v(99.45, -56.32) * mm});
            skArc(sketch, "E8.37.4", {"start": v(105.85, -50.3) * mm, "mid": v(104.24, -50.17) * mm, "end": v(102.63, -50.3) * mm});
            skArc(sketch, "E8.37.5", {"start": v(107.08, -50.48) * mm, "mid": v(108.58, -50.54) * mm, "end": v(110.06, -50.26) * mm});
            skLineSegment(sketch, "E8.37.6", {"start": v(105.85, -50.3) * mm, "end": v(107.08, -50.48) * mm});
            skLineSegment(sketch, "E8.37.7", {"start": v(101.26, -58.98) * mm, "end": v(102.11, -59.89) * mm});
            skArc(sketch, "E8.38.0", {"start": v(107.7, -38.27) * mm, "mid": v(105.97, -39.2) * mm, "end": v(104.85, -40.82) * mm});
            skArc(sketch, "E8.38.1", {"start": v(108.27, -47.86) * mm, "mid": v(109.3, -48.96) * mm, "end": v(110.06, -50.26) * mm});
            skArc(sketch, "E8.38.2", {"start": v(105.22, -44.62) * mm, "mid": v(104.58, -42.76) * mm, "end": v(104.85, -40.82) * mm});
            skArc(sketch, "E8.38.3", {"start": v(107.33, -47.06) * mm, "mid": v(106.19, -45.92) * mm, "end": v(105.22, -44.62) * mm});
            skArc(sketch, "E8.38.4", {"start": v(110.9, -37.9) * mm, "mid": v(109.28, -37.96) * mm, "end": v(107.7, -38.27) * mm});
            skArc(sketch, "E8.38.5", {"start": v(112.13, -37.94) * mm, "mid": v(113.64, -37.83) * mm, "end": v(115.08, -37.39) * mm});
            skLineSegment(sketch, "E8.38.6", {"start": v(110.9, -37.9) * mm, "end": v(112.13, -37.94) * mm});
            skLineSegment(sketch, "E8.38.7", {"start": v(107.33, -47.06) * mm, "end": v(108.27, -47.86) * mm});
            skArc(sketch, "E8.39.0", {"start": v(111.36, -25.74) * mm, "mid": v(109.74, -26.87) * mm, "end": v(108.82, -28.6) * mm});
            skArc(sketch, "E8.39.1", {"start": v(113.02, -35.2) * mm, "mid": v(114.17, -36.18) * mm, "end": v(115.08, -37.39) * mm});
            skArc(sketch, "E8.39.2", {"start": v(109.63, -32.33) * mm, "mid": v(108.77, -30.56) * mm, "end": v(108.82, -28.6) * mm});
            skArc(sketch, "E8.39.3", {"start": v(112, -34.52) * mm, "mid": v(110.73, -33.51) * mm, "end": v(109.63, -32.33) * mm});
            skArc(sketch, "E8.39.4", {"start": v(114.5, -25) * mm, "mid": v(112.9, -25.26) * mm, "end": v(111.36, -25.74) * mm});
            skArc(sketch, "E8.39.5", {"start": v(115.73, -24.91) * mm, "mid": v(117.2, -24.63) * mm, "end": v(118.59, -24.02) * mm});
            skLineSegment(sketch, "E8.39.6", {"start": v(114.5, -25) * mm, "end": v(115.73, -24.91) * mm});
            skLineSegment(sketch, "E8.39.7", {"start": v(112, -34.52) * mm, "end": v(113.02, -35.2) * mm});
            skArc(sketch, "E8.40.0", {"start": v(113.57, -12.88) * mm, "mid": v(112.1, -14.18) * mm, "end": v(111.37, -16) * mm});
            skArc(sketch, "E8.40.1", {"start": v(116.3, -22.1) * mm, "mid": v(117.55, -22.93) * mm, "end": v(118.59, -24.02) * mm});
            skArc(sketch, "E8.40.2", {"start": v(112.6, -19.63) * mm, "mid": v(111.55, -17.96) * mm, "end": v(111.37, -16) * mm});
            skArc(sketch, "E8.40.3", {"start": v(115.2, -21.52) * mm, "mid": v(113.83, -20.67) * mm, "end": v(112.6, -19.63) * mm});
            skArc(sketch, "E8.40.4", {"start": v(116.6, -11.8) * mm, "mid": v(115.04, -12.23) * mm, "end": v(113.57, -12.88) * mm});
            skArc(sketch, "E8.40.5", {"start": v(117.81, -11.56) * mm, "mid": v(119.25, -11.1) * mm, "end": v(120.55, -10.35) * mm});
            skLineSegment(sketch, "E8.40.6", {"start": v(116.6, -11.8) * mm, "end": v(117.81, -11.56) * mm});
            skLineSegment(sketch, "E8.40.7", {"start": v(115.2, -21.52) * mm, "end": v(116.3, -22.1) * mm});
            skArc(sketch, "E8.41.0", {"start": v(114.3, 0.15) * mm, "mid": v(112.98, -1.31) * mm, "end": v(112.47, -3.2) * mm});
            skArc(sketch, "E8.41.1", {"start": v(118.06, -8.7) * mm, "mid": v(119.4, -9.38) * mm, "end": v(120.55, -10.35) * mm});
            skArc(sketch, "E8.41.2", {"start": v(114.1, -6.66) * mm, "mid": v(112.87, -5.13) * mm, "end": v(112.47, -3.2) * mm});
            skArc(sketch, "E8.41.3", {"start": v(116.9, -8.25) * mm, "mid": v(115.44, -7.56) * mm, "end": v(114.1, -6.66) * mm});
            skArc(sketch, "E8.41.4", {"start": v(117.18, 1.57) * mm, "mid": v(115.69, 0.97) * mm, "end": v(114.3, 0.15) * mm});
            skArc(sketch, "E8.41.5", {"start": v(118.36, 1.95) * mm, "mid": v(119.74, 2.56) * mm, "end": v(120.95, 3.46) * mm});
            skLineSegment(sketch, "E8.41.6", {"start": v(117.18, 1.57) * mm, "end": v(118.36, 1.95) * mm});
            skLineSegment(sketch, "E8.41.7", {"start": v(116.9, -8.25) * mm, "end": v(118.06, -8.7) * mm});
            skArc(sketch, "E8.42.0", {"start": v(113.53, 13.18) * mm, "mid": v(112.4, 11.58) * mm, "end": v(112.1, 9.63) * mm});
            skArc(sketch, "E8.42.1", {"start": v(118.28, 4.82) * mm, "mid": v(119.7, 4.3) * mm, "end": v(120.95, 3.46) * mm});
            skArc(sketch, "E8.42.2", {"start": v(114.12, 6.39) * mm, "mid": v(112.72, 7.77) * mm, "end": v(112.1, 9.63) * mm});
            skArc(sketch, "E8.42.3", {"start": v(117.08, 5.13) * mm, "mid": v(115.55, 5.65) * mm, "end": v(114.12, 6.39) * mm});
            skArc(sketch, "E8.42.4", {"start": v(116.24, 14.92) * mm, "mid": v(114.82, 14.15) * mm, "end": v(113.53, 13.18) * mm});
            skArc(sketch, "E8.42.5", {"start": v(117.37, 15.43) * mm, "mid": v(118.67, 16.19) * mm, "end": v(119.77, 17.22) * mm});
            skLineSegment(sketch, "E8.42.6", {"start": v(116.24, 14.92) * mm, "end": v(117.37, 15.43) * mm});
            skLineSegment(sketch, "E8.42.7", {"start": v(117.08, 5.13) * mm, "end": v(118.28, 4.82) * mm});
            skArc(sketch, "E8.43.0", {"start": v(111.3, 26.03) * mm, "mid": v(110.34, 24.31) * mm, "end": v(110.27, 22.35) * mm});
            skArc(sketch, "E8.43.1", {"start": v(116.96, 18.28) * mm, "mid": v(118.42, 17.9) * mm, "end": v(119.77, 17.22) * mm});
            skArc(sketch, "E8.43.2", {"start": v(112.65, 19.35) * mm, "mid": v(111.1, 20.57) * mm, "end": v(110.27, 22.35) * mm});
            skArc(sketch, "E8.43.3", {"start": v(115.73, 18.44) * mm, "mid": v(114.16, 18.78) * mm, "end": v(112.65, 19.35) * mm});
            skArc(sketch, "E8.43.4", {"start": v(113.78, 28.07) * mm, "mid": v(112.46, 27.15) * mm, "end": v(111.3, 26.03) * mm});
            skArc(sketch, "E8.43.5", {"start": v(114.85, 28.7) * mm, "mid": v(116.05, 29.61) * mm, "end": v(117.02, 30.76) * mm});
            skLineSegment(sketch, "E8.43.6", {"start": v(113.78, 28.07) * mm, "end": v(114.85, 28.7) * mm});
            skLineSegment(sketch, "E8.43.7", {"start": v(115.73, 18.44) * mm, "end": v(116.96, 18.28) * mm});
            skArc(sketch, "E8.44.0", {"start": v(107.6, 38.55) * mm, "mid": v(106.85, 36.73) * mm, "end": v(107, 34.77) * mm});
            skArc(sketch, "E8.44.1", {"start": v(114.12, 31.49) * mm, "mid": v(115.61, 31.3) * mm, "end": v(117.02, 30.76) * mm});
            skArc(sketch, "E8.44.2", {"start": v(109.7, 32.07) * mm, "mid": v(108.03, 33.1) * mm, "end": v(107, 34.77) * mm});
            skArc(sketch, "E8.44.3", {"start": v(112.88, 31.51) * mm, "mid": v(111.27, 31.67) * mm, "end": v(109.7, 32.07) * mm});
            skArc(sketch, "E8.44.4", {"start": v(109.84, 40.86) * mm, "mid": v(108.63, 39.79) * mm, "end": v(107.6, 38.55) * mm});
            skArc(sketch, "E8.44.5", {"start": v(110.83, 41.6) * mm, "mid": v(111.92, 42.65) * mm, "end": v(112.75, 43.9) * mm});
            skLineSegment(sketch, "E8.44.6", {"start": v(109.84, 40.86) * mm, "end": v(110.83, 41.6) * mm});
            skLineSegment(sketch, "E8.44.7", {"start": v(112.88, 31.51) * mm, "end": v(114.12, 31.49) * mm});
            skArc(sketch, "E8.45.0", {"start": v(102.5, 50.56) * mm, "mid": v(101.97, 48.67) * mm, "end": v(102.34, 46.74) * mm});
            skArc(sketch, "E8.45.1", {"start": v(109.78, 44.3) * mm, "mid": v(111.3, 44.27) * mm, "end": v(112.75, 43.9) * mm});
            skArc(sketch, "E8.45.2", {"start": v(105.34, 44.36) * mm, "mid": v(103.56, 45.2) * mm, "end": v(102.34, 46.74) * mm});
            skArc(sketch, "E8.45.3", {"start": v(108.55, 44.17) * mm, "mid": v(106.94, 44.15) * mm, "end": v(105.34, 44.36) * mm});
            skArc(sketch, "E8.45.4", {"start": v(104.47, 53.12) * mm, "mid": v(103.4, 51.91) * mm, "end": v(102.5, 50.56) * mm});
            skArc(sketch, "E8.45.5", {"start": v(105.36, 53.97) * mm, "mid": v(106.33, 55.13) * mm, "end": v(107.01, 56.47) * mm});
            skLineSegment(sketch, "E8.45.6", {"start": v(104.47, 53.12) * mm, "end": v(105.36, 53.97) * mm});
            skLineSegment(sketch, "E8.45.7", {"start": v(108.55, 44.17) * mm, "end": v(109.78, 44.3) * mm});
            skArc(sketch, "E8.46.0", {"start": v(96.07, 61.92) * mm, "mid": v(95.76, 59.98) * mm, "end": v(96.35, 58.1) * mm});
            skArc(sketch, "E8.46.1", {"start": v(104.02, 56.52) * mm, "mid": v(105.52, 56.66) * mm, "end": v(107.01, 56.47) * mm});
            skArc(sketch, "E8.46.2", {"start": v(99.6, 56.08) * mm, "mid": v(97.73, 56.7) * mm, "end": v(96.35, 58.1) * mm});
            skArc(sketch, "E8.46.3", {"start": v(102.8, 56.26) * mm, "mid": v(101.2, 56.05) * mm, "end": v(99.6, 56.08) * mm});
            skArc(sketch, "E8.46.4", {"start": v(97.73, 64.68) * mm, "mid": v(96.8, 63.36) * mm, "end": v(96.07, 61.92) * mm});
            skArc(sketch, "E8.46.5", {"start": v(98.52, 65.63) * mm, "mid": v(99.35, 66.89) * mm, "end": v(99.88, 68.3) * mm});
            skLineSegment(sketch, "E8.46.6", {"start": v(97.73, 64.68) * mm, "end": v(98.52, 65.63) * mm});
            skLineSegment(sketch, "E8.46.7", {"start": v(102.8, 56.26) * mm, "end": v(104.02, 56.52) * mm});
            skArc(sketch, "E8.47.0", {"start": v(88.4, 72.47) * mm, "mid": v(88.3, 70.5) * mm, "end": v(89.1, 68.71) * mm});
            skArc(sketch, "E8.47.1", {"start": v(96.9, 68) * mm, "mid": v(98.37, 68.32) * mm, "end": v(99.88, 68.3) * mm});
            skArc(sketch, "E8.47.2", {"start": v(92.55, 67.07) * mm, "mid": v(90.63, 67.48) * mm, "end": v(89.1, 68.71) * mm});
            skArc(sketch, "E8.47.3", {"start": v(95.72, 67.61) * mm, "mid": v(94.16, 67.22) * mm, "end": v(92.55, 67.07) * mm});
            skArc(sketch, "E8.47.4", {"start": v(89.72, 75.4) * mm, "mid": v(88.95, 73.98) * mm, "end": v(88.4, 72.47) * mm});
            skArc(sketch, "E8.47.5", {"start": v(90.4, 76.43) * mm, "mid": v(91.08, 77.78) * mm, "end": v(91.44, 79.24) * mm});
            skLineSegment(sketch, "E8.47.6", {"start": v(89.72, 75.4) * mm, "end": v(90.4, 76.43) * mm});
            skLineSegment(sketch, "E8.47.7", {"start": v(95.72, 67.61) * mm, "end": v(96.9, 68) * mm});
            skArc(sketch, "E8.48.0", {"start": v(79.55, 82.07) * mm, "mid": v(79.68, 80.1) * mm, "end": v(80.69, 78.42) * mm});
            skArc(sketch, "E8.48.1", {"start": v(88.52, 78.6) * mm, "mid": v(89.94, 79.1) * mm, "end": v(91.44, 79.24) * mm});
            skArc(sketch, "E8.48.2", {"start": v(84.3, 77.18) * mm, "mid": v(82.35, 77.37) * mm, "end": v(80.69, 78.42) * mm});
            skArc(sketch, "E8.48.3", {"start": v(87.4, 78.08) * mm, "mid": v(85.88, 77.52) * mm, "end": v(84.3, 77.18) * mm});
            skArc(sketch, "E8.48.4", {"start": v(80.54, 85.13) * mm, "mid": v(79.94, 83.64) * mm, "end": v(79.55, 82.07) * mm});
            skArc(sketch, "E8.48.5", {"start": v(81.1, 86.24) * mm, "mid": v(81.62, 87.65) * mm, "end": v(81.82, 89.15) * mm});
            skLineSegment(sketch, "E8.48.6", {"start": v(80.54, 85.13) * mm, "end": v(81.1, 86.24) * mm});
            skLineSegment(sketch, "E8.48.7", {"start": v(87.4, 78.08) * mm, "end": v(88.52, 78.6) * mm});
            skArc(sketch, "E8.49.0", {"start": v(69.68, 90.6) * mm, "mid": v(70.03, 88.67) * mm, "end": v(71.22, 87.1) * mm});
            skArc(sketch, "E8.49.1", {"start": v(78.98, 88.19) * mm, "mid": v(80.34, 88.83) * mm, "end": v(81.82, 89.15) * mm});
            skArc(sketch, "E8.49.2", {"start": v(74.96, 86.29) * mm, "mid": v(73, 86.25) * mm, "end": v(71.22, 87.1) * mm});
            skArc(sketch, "E8.49.3", {"start": v(77.92, 87.54) * mm, "mid": v(76.49, 86.8) * mm, "end": v(74.96, 86.29) * mm});
            skArc(sketch, "E8.49.4", {"start": v(70.31, 93.76) * mm, "mid": v(69.88, 92.2) * mm, "end": v(69.68, 90.6) * mm});
            skArc(sketch, "E8.49.5", {"start": v(70.74, 94.92) * mm, "mid": v(71.1, 96.39) * mm, "end": v(71.12, 97.9) * mm});
            skLineSegment(sketch, "E8.49.6", {"start": v(70.31, 93.76) * mm, "end": v(70.74, 94.92) * mm});
            skLineSegment(sketch, "E8.49.7", {"start": v(77.92, 87.54) * mm, "end": v(78.98, 88.19) * mm});
            skArc(sketch, "E8.50.0", {"start": v(58.9, 97.96) * mm, "mid": v(59.47, 96.07) * mm, "end": v(60.83, 94.66) * mm});
            skArc(sketch, "E8.50.1", {"start": v(68.41, 96.61) * mm, "mid": v(69.7, 97.4) * mm, "end": v(71.12, 97.9) * mm});
            skArc(sketch, "E8.50.2", {"start": v(64.63, 94.27) * mm, "mid": v(62.68, 94) * mm, "end": v(60.83, 94.66) * mm});
            skArc(sketch, "E8.50.3", {"start": v(67.44, 95.85) * mm, "mid": v(66.1, 94.96) * mm, "end": v(64.63, 94.27) * mm});
            skArc(sketch, "E8.50.4", {"start": v(59.17, 101.16) * mm, "mid": v(58.91, 99.57) * mm, "end": v(58.9, 97.96) * mm});
            skArc(sketch, "E8.50.5", {"start": v(59.46, 102.37) * mm, "mid": v(59.65, 103.86) * mm, "end": v(59.5, 105.36) * mm});
            skLineSegment(sketch, "E8.50.6", {"start": v(59.17, 101.16) * mm, "end": v(59.46, 102.37) * mm});
            skLineSegment(sketch, "E8.50.7", {"start": v(67.44, 95.85) * mm, "end": v(68.41, 96.61) * mm});
            skArc(sketch, "E8.51.0", {"start": v(47.35, 104.03) * mm, "mid": v(48.13, 102.23) * mm, "end": v(49.64, 100.97) * mm});
            skArc(sketch, "E8.51.1", {"start": v(56.95, 103.78) * mm, "mid": v(58.14, 104.72) * mm, "end": v(59.5, 105.36) * mm});
            skArc(sketch, "E8.51.2", {"start": v(53.46, 101.02) * mm, "mid": v(51.56, 100.54) * mm, "end": v(49.64, 100.97) * mm});
            skArc(sketch, "E8.51.3", {"start": v(56.07, 102.91) * mm, "mid": v(54.84, 101.87) * mm, "end": v(53.46, 101.02) * mm});
            skArc(sketch, "E8.51.4", {"start": v(47.25, 107.25) * mm, "mid": v(47.18, 105.64) * mm, "end": v(47.35, 104.03) * mm});
            skArc(sketch, "E8.51.5", {"start": v(47.4, 108.48) * mm, "mid": v(47.42, 109.99) * mm, "end": v(47.1, 111.46) * mm});
            skLineSegment(sketch, "E8.51.6", {"start": v(47.25, 107.25) * mm, "end": v(47.4, 108.48) * mm});
            skLineSegment(sketch, "E8.51.7", {"start": v(56.07, 102.91) * mm, "end": v(56.95, 103.78) * mm});
            skArc(sketch, "E8.52.0", {"start": v(35.18, 108.75) * mm, "mid": v(36.16, 107.05) * mm, "end": v(37.8, 105.97) * mm});
            skArc(sketch, "E8.52.1", {"start": v(44.75, 109.6) * mm, "mid": v(45.82, 110.66) * mm, "end": v(47.1, 111.46) * mm});
            skArc(sketch, "E8.52.2", {"start": v(41.6, 106.46) * mm, "mid": v(39.76, 105.76) * mm, "end": v(37.8, 105.97) * mm});
            skArc(sketch, "E8.52.3", {"start": v(43.98, 108.63) * mm, "mid": v(42.87, 107.46) * mm, "end": v(41.6, 106.46) * mm});
            skArc(sketch, "E8.52.4", {"start": v(34.72, 111.94) * mm, "mid": v(34.83, 110.33) * mm, "end": v(35.18, 108.75) * mm});
            skArc(sketch, "E8.52.5", {"start": v(34.73, 113.18) * mm, "mid": v(34.57, 114.67) * mm, "end": v(34.09, 116.1) * mm});
            skLineSegment(sketch, "E8.52.6", {"start": v(34.72, 111.94) * mm, "end": v(34.73, 113.18) * mm});
            skLineSegment(sketch, "E8.52.7", {"start": v(43.98, 108.63) * mm, "end": v(44.75, 109.6) * mm});
            skArc(sketch, "E8.53.0", {"start": v(22.56, 112.05) * mm, "mid": v(23.73, 110.47) * mm, "end": v(25.48, 109.6) * mm});
            skArc(sketch, "E8.53.1", {"start": v(31.97, 113.99) * mm, "mid": v(32.9, 115.16) * mm, "end": v(34.09, 116.1) * mm});
            skArc(sketch, "E8.53.2", {"start": v(29.2, 110.5) * mm, "mid": v(27.45, 109.6) * mm, "end": v(25.48, 109.6) * mm});
            skArc(sketch, "E8.53.3", {"start": v(31.3, 112.94) * mm, "mid": v(30.34, 111.65) * mm, "end": v(29.2, 110.5) * mm});
            skArc(sketch, "E8.53.4", {"start": v(21.73, 115.16) * mm, "mid": v(22.03, 113.58) * mm, "end": v(22.56, 112.05) * mm});
            skArc(sketch, "E8.53.5", {"start": v(21.6, 116.4) * mm, "mid": v(21.28, 117.87) * mm, "end": v(20.63, 119.23) * mm});
            skLineSegment(sketch, "E8.53.6", {"start": v(21.73, 115.16) * mm, "end": v(21.6, 116.4) * mm});
            skLineSegment(sketch, "E8.53.7", {"start": v(31.3, 112.94) * mm, "end": v(31.97, 113.99) * mm});
            skArc(sketch, "E8.54.0", {"start": v(9.64, 113.9) * mm, "mid": v(10.98, 112.46) * mm, "end": v(12.83, 111.78) * mm});
            skArc(sketch, "E8.54.1", {"start": v(18.77, 116.89) * mm, "mid": v(19.57, 118.16) * mm, "end": v(20.63, 119.23) * mm});
            skArc(sketch, "E8.54.2", {"start": v(16.4, 113.12) * mm, "mid": v(14.78, 112.02) * mm, "end": v(12.83, 111.78) * mm});
            skArc(sketch, "E8.54.3", {"start": v(18.23, 115.77) * mm, "mid": v(17.42, 114.38) * mm, "end": v(16.4, 113.12) * mm});
            skArc(sketch, "E8.54.4", {"start": v(8.46, 116.9) * mm, "mid": v(8.94, 115.35) * mm, "end": v(9.64, 113.9) * mm});
            skArc(sketch, "E8.54.5", {"start": v(8.2, 118.1) * mm, "mid": v(7.7, 119.53) * mm, "end": v(6.9, 120.8) * mm});
            skLineSegment(sketch, "E8.54.6", {"start": v(8.46, 116.9) * mm, "end": v(8.2, 118.1) * mm});
            skLineSegment(sketch, "E8.54.7", {"start": v(18.23, 115.77) * mm, "end": v(18.77, 116.89) * mm});
            skPoint(sketch, "E8.center", {"position": v(0, 0) * mm});
            skCircle(sketch, "E9", {"center": v(0, 0) * mm, "radius": 119.3 * mm});
            skCircle(sketch, "E10", {"center": v(0, 0) * mm, "radius": 68.25 * mm});
            skCircle(sketch, "E11", {"center": v(0, 0) * mm, "radius": 109.9 * mm});
            skCircle(sketch, "E12", {"center": v(0, 75.6) * mm, "radius": 5.25 * mm});
            skCircle(sketch, "E13.1.0", {"center": v(-71.9, 23.37) * mm, "radius": 5.25 * mm});
            skCircle(sketch, "E13.2.0", {"center": v(-44.44, -61.16) * mm, "radius": 5.25 * mm});
            skCircle(sketch, "E13.3.0", {"center": v(44.44, -61.16) * mm, "radius": 5.25 * mm});
            skCircle(sketch, "E13.4.0", {"center": v(71.9, 23.37) * mm, "radius": 5.25 * mm});
            skSolve(sketch);
        }
        {
            var Q0;
            Q0=makeQuery(id+"F0.imprint","IMPRINT",FACE,{"disambiguationData":[TD([[makeQuery(id+"F0.imprint","IMPRINT",EDGE,{"derivedFrom":sQuery(id+"F0.wireOp",EDGE,"E10")}),-1.0]])]});
            extrude(context, id + "F1", {"entities" : qUnion([Q0]), "endBound" : BoundingType.SYMMETRIC, "depth" : 4.22 * mm});
        }
        {
            var Q0;
            Q0=makeQuery(id+"F0.imprint","IMPRINT",FACE,{"disambiguationData":[TD([[makeQuery(id+"F0.imprint","IMPRINT",EDGE,{"derivedFrom":sQuery(id+"F0.wireOp",EDGE,"E0")}),-1.0]])]});
            extrude(context, id + "F2", {"entities" : qUnion([Q0]), "operationType" : NewBodyOperationType.ADD, "endBound" : BoundingType.SYMMETRIC, "depth" : 3.2 * mm});
        }
        {
            var Q0;
            Q0=makeQuery(id+"F1.opExtrude","CAP_FACE",FACE,{"disambiguationData":[OSD([sQuery(id+"F0.wireOp",EDGE,"E10"),sQuery(id+"F0.wireOp",EDGE,"E11"),sQuery(id+"F0.wireOp",EDGE,"E12"),sQuery(id+"F0.wireOp",EDGE,"E13.1.0"),sQuery(id+"F0.wireOp",EDGE,"E13.2.0"),sQuery(id+"F0.wireOp",EDGE,"E13.3.0"),sQuery(id+"F0.wireOp",EDGE,"E13.4.0")])],"isStart":false});
            var sketch = newSketch(context, id + "F3", { "sketchPlane" : qUnion([Q0])});
            skLineSegment(sketch, "E14", {"start": v(50.8, -52.87) * mm, "end": v(72.62, -75.58) * mm});
            skLineSegment(sketch, "E15", {"start": v(72.18, 12.92) * mm, "end": v(103.17, 18.47) * mm});
            skArc(sketch, "E16", {"start": v(72.62, -75.58) * mm, "mid": v(77.8, -70.24) * mm, "end": v(82.58, -64.55) * mm});
            skArc(sketch, "E17", {"start": v(50.8, -52.87) * mm, "mid": v(54.42, -49.14) * mm, "end": v(57.77, -45.16) * mm});
            skLineSegment(sketch, "E18", {"start": v(73.28, 2.58) * mm, "end": v(104.75, 3.7) * mm});
            skLineSegment(sketch, "E19", {"start": v(73.32, 0.66) * mm, "end": v(104.8, 0.95) * mm});
            skArc(sketch, "E20.trimOffspring", {"start": v(104.75, 3.7) * mm, "mid": v(104.22, 11.1) * mm, "end": v(103.17, 18.47) * mm});
            skArc(sketch, "E21.trimOffspring", {"start": v(73.28, 2.58) * mm, "mid": v(72.91, 7.77) * mm, "end": v(72.18, 12.92) * mm});
            skLineSegment(sketch, "E22", {"start": v(72.68, -9.72) * mm, "end": v(103.89, -13.89) * mm});
            skArc(sketch, "E23.trimOffspring", {"start": v(72.68, -9.72) * mm, "mid": v(73.18, -4.54) * mm, "end": v(73.32, 0.66) * mm});
            skArc(sketch, "E24.trimOffspring", {"start": v(103.89, -13.89) * mm, "mid": v(104.61, -6.49) * mm, "end": v(104.8, 0.95) * mm});
            skLineSegment(sketch, "E25", {"start": v(70.03, -21.74) * mm, "end": v(100.1, -31.08) * mm});
            skLineSegment(sketch, "E26", {"start": v(69.44, -23.57) * mm, "end": v(99.25, -33.69) * mm});
            skArc(sketch, "E27.trimOffspring", {"start": v(70.03, -21.74) * mm, "mid": v(71.4, -16.72) * mm, "end": v(72.4, -11.62) * mm});
            skArc(sketch, "E28.trimOffspring", {"start": v(100.1, -31.08) * mm, "mid": v(102.05, -23.9) * mm, "end": v(103.49, -16.6) * mm});
            skLineSegment(sketch, "E29", {"start": v(65.4, -33.15) * mm, "end": v(93.49, -47.39) * mm});
            skLineSegment(sketch, "E30", {"start": v(64.51, -34.85) * mm, "end": v(92.21, -49.82) * mm});
            skArc(sketch, "E31.trimOffspring", {"start": v(65.4, -33.15) * mm, "mid": v(67.59, -28.43) * mm, "end": v(69.44, -23.57) * mm});
            skArc(sketch, "E32.trimOffspring", {"start": v(93.49, -47.39) * mm, "mid": v(96.61, -40.64) * mm, "end": v(99.25, -33.69) * mm});
            skLineSegment(sketch, "E33", {"start": v(58.93, -43.63) * mm, "end": v(84.24, -62.36) * mm});
            skLineSegment(sketch, "E34", {"start": v(57.77, -45.16) * mm, "end": v(82.58, -64.55) * mm});
            skArc(sketch, "E35.trimOffspring", {"start": v(58.93, -43.63) * mm, "mid": v(61.88, -39.34) * mm, "end": v(64.51, -34.85) * mm});
            skArc(sketch, "E36.trimOffspring", {"start": v(84.24, -62.36) * mm, "mid": v(88.45, -56.23) * mm, "end": v(92.21, -49.82) * mm});
            skLineSegment(sketch, "E37", {"start": v(72.4, -11.62) * mm, "end": v(103.49, -16.6) * mm});
            skLineSegment(sketch, "E38.1.0", {"start": v(42.32, 59.88) * mm, "end": v(60.49, 85.6) * mm});
            skArc(sketch, "E38.1.1", {"start": v(31.7, 66.12) * mm, "mid": v(26.93, 68.2) * mm, "end": v(22.03, 69.94) * mm});
            skArc(sketch, "E38.1.2", {"start": v(45.31, 94.51) * mm, "mid": v(38.5, 97.49) * mm, "end": v(31.49, 99.97) * mm});
            skLineSegment(sketch, "E38.1.3", {"start": v(33.42, 65.27) * mm, "end": v(47.77, 93.3) * mm});
            skLineSegment(sketch, "E38.1.4", {"start": v(31.7, 66.12) * mm, "end": v(45.31, 94.51) * mm});
            skLineSegment(sketch, "E38.1.5", {"start": v(51.74, 51.96) * mm, "end": v(73.96, 74.27) * mm});
            skArc(sketch, "E38.1.6", {"start": v(20.19, 70.5) * mm, "mid": v(15.14, 71.75) * mm, "end": v(10.01, 72.64) * mm});
            skArc(sketch, "E38.1.7", {"start": v(85.34, 60.85) * mm, "mid": v(80.81, 66.74) * mm, "end": v(75.88, 72.3) * mm});
            skLineSegment(sketch, "E38.1.8", {"start": v(43.87, 58.75) * mm, "end": v(62.7, 83.98) * mm});
            skArc(sketch, "E38.1.9", {"start": v(73.96, 74.27) * mm, "mid": v(68.5, 79.33) * mm, "end": v(62.7, 83.98) * mm});
            skArc(sketch, "E38.1.10", {"start": v(28.86, 100.76) * mm, "mid": v(21.64, 102.55) * mm, "end": v(14.31, 103.83) * mm});
            skLineSegment(sketch, "E38.1.11", {"start": v(22.03, 69.94) * mm, "end": v(31.49, 99.97) * mm});
            skLineSegment(sketch, "E38.1.12", {"start": v(53.08, 50.59) * mm, "end": v(75.88, 72.3) * mm});
            skLineSegment(sketch, "E38.1.13", {"start": v(59.7, 42.57) * mm, "end": v(85.34, 60.85) * mm});
            skLineSegment(sketch, "E38.1.14", {"start": v(20.19, 70.5) * mm, "end": v(28.86, 100.76) * mm});
            skArc(sketch, "E38.1.15", {"start": v(94.32, 45.7) * mm, "mid": v(90.84, 52.28) * mm, "end": v(86.9, 58.6) * mm});
            skLineSegment(sketch, "E38.1.16", {"start": v(10.01, 72.64) * mm, "end": v(14.31, 103.83) * mm});
            skArc(sketch, "E38.1.17", {"start": v(51.74, 51.96) * mm, "mid": v(47.93, 55.5) * mm, "end": v(43.87, 58.75) * mm});
            skLineSegment(sketch, "E38.1.18", {"start": v(65.98, 31.98) * mm, "end": v(94.32, 45.7) * mm});
            skArc(sketch, "E38.1.19", {"start": v(60.49, 85.6) * mm, "mid": v(54.27, 89.67) * mm, "end": v(47.77, 93.3) * mm});
            skArc(sketch, "E38.1.20", {"start": v(42.32, 59.88) * mm, "mid": v(37.96, 62.73) * mm, "end": v(33.42, 65.27) * mm});
            skLineSegment(sketch, "E38.1.21", {"start": v(60.8, 41) * mm, "end": v(86.9, 58.6) * mm});
            skLineSegment(sketch, "E38.1.22", {"start": v(31.7, 66.12) * mm, "end": v(45.31, 94.51) * mm});
            skArc(sketch, "E38.1.23", {"start": v(65.98, 31.98) * mm, "mid": v(63.55, 36.58) * mm, "end": v(60.8, 41) * mm});
            skArc(sketch, "E38.1.24", {"start": v(59.7, 42.57) * mm, "mid": v(56.54, 46.7) * mm, "end": v(53.08, 50.59) * mm});
            skLineSegment(sketch, "E38.2.0", {"start": v(-43.88, 58.75) * mm, "end": v(-62.72, 83.98) * mm});
            skArc(sketch, "E38.2.1", {"start": v(-53.09, 50.58) * mm, "mid": v(-56.54, 46.69) * mm, "end": v(-59.7, 42.56) * mm});
            skArc(sketch, "E38.2.2", {"start": v(-75.88, 72.3) * mm, "mid": v(-80.82, 66.74) * mm, "end": v(-85.35, 60.84) * mm});
            skLineSegment(sketch, "E38.2.3", {"start": v(-51.74, 51.95) * mm, "end": v(-73.96, 74.26) * mm});
            skLineSegment(sketch, "E38.2.4", {"start": v(-53.09, 50.58) * mm, "end": v(-75.88, 72.3) * mm});
            skLineSegment(sketch, "E38.2.5", {"start": v(-33.43, 65.26) * mm, "end": v(-47.78, 93.29) * mm});
            skArc(sketch, "E38.2.6", {"start": v(-60.8, 40.98) * mm, "mid": v(-63.56, 36.57) * mm, "end": v(-65.99, 31.97) * mm});
            skArc(sketch, "E38.2.7", {"start": v(-31.5, 99.97) * mm, "mid": v(-38.5, 97.48) * mm, "end": v(-45.32, 94.5) * mm});
            skLineSegment(sketch, "E38.2.8", {"start": v(-42.32, 59.88) * mm, "end": v(-60.5, 85.6) * mm});
            skArc(sketch, "E38.2.9", {"start": v(-47.78, 93.29) * mm, "mid": v(-54.27, 89.66) * mm, "end": v(-60.5, 85.6) * mm});
            skArc(sketch, "E38.2.10", {"start": v(-86.91, 58.58) * mm, "mid": v(-90.85, 52.27) * mm, "end": v(-94.32, 45.7) * mm});
            skLineSegment(sketch, "E38.2.11", {"start": v(-59.7, 42.56) * mm, "end": v(-85.35, 60.84) * mm});
            skLineSegment(sketch, "E38.2.12", {"start": v(-31.7, 66.12) * mm, "end": v(-45.32, 94.5) * mm});
            skLineSegment(sketch, "E38.2.13", {"start": v(-22.04, 69.94) * mm, "end": v(-31.5, 99.97) * mm});
            skLineSegment(sketch, "E38.2.14", {"start": v(-60.8, 40.98) * mm, "end": v(-86.91, 58.58) * mm});
            skArc(sketch, "E38.2.15", {"start": v(-14.33, 103.83) * mm, "mid": v(-21.65, 102.55) * mm, "end": v(-28.87, 100.76) * mm});
            skLineSegment(sketch, "E38.2.16", {"start": v(-65.99, 31.97) * mm, "end": v(-94.32, 45.7) * mm});
            skArc(sketch, "E38.2.17", {"start": v(-33.43, 65.26) * mm, "mid": v(-37.97, 62.73) * mm, "end": v(-42.32, 59.88) * mm});
            skLineSegment(sketch, "E38.2.18", {"start": v(-10.02, 72.64) * mm, "end": v(-14.33, 103.83) * mm});
            skArc(sketch, "E38.2.19", {"start": v(-62.72, 83.98) * mm, "mid": v(-68.51, 79.32) * mm, "end": v(-73.96, 74.26) * mm});
            skArc(sketch, "E38.2.20", {"start": v(-43.88, 58.75) * mm, "mid": v(-47.93, 55.5) * mm, "end": v(-51.74, 51.95) * mm});
            skLineSegment(sketch, "E38.2.21", {"start": v(-20.2, 70.49) * mm, "end": v(-28.87, 100.76) * mm});
            skLineSegment(sketch, "E38.2.22", {"start": v(-53.09, 50.58) * mm, "end": v(-75.88, 72.3) * mm});
            skArc(sketch, "E38.2.23", {"start": v(-10.02, 72.64) * mm, "mid": v(-15.15, 71.74) * mm, "end": v(-20.2, 70.49) * mm});
            skArc(sketch, "E38.2.24", {"start": v(-22.04, 69.94) * mm, "mid": v(-26.94, 68.2) * mm, "end": v(-31.7, 66.12) * mm});
            skLineSegment(sketch, "E38.3.0", {"start": v(-69.43, -23.57) * mm, "end": v(-99.25, -33.7) * mm});
            skArc(sketch, "E38.3.1", {"start": v(-64.5, -34.86) * mm, "mid": v(-61.88, -39.35) * mm, "end": v(-58.93, -43.63) * mm});
            skArc(sketch, "E38.3.2", {"start": v(-92.2, -49.83) * mm, "mid": v(-88.44, -56.24) * mm, "end": v(-84.23, -62.37) * mm});
            skLineSegment(sketch, "E38.3.3", {"start": v(-65.4, -33.16) * mm, "end": v(-93.48, -47.4) * mm});
            skLineSegment(sketch, "E38.3.4", {"start": v(-64.5, -34.86) * mm, "end": v(-92.2, -49.83) * mm});
            skLineSegment(sketch, "E38.3.5", {"start": v(-72.4, -11.62) * mm, "end": v(-103.49, -16.61) * mm});
            skArc(sketch, "E38.3.6", {"start": v(-57.77, -45.16) * mm, "mid": v(-54.42, -49.14) * mm, "end": v(-50.8, -52.88) * mm});
            skArc(sketch, "E38.3.7", {"start": v(-104.8, 0.94) * mm, "mid": v(-104.6, -6.5) * mm, "end": v(-103.89, -13.9) * mm});
            skLineSegment(sketch, "E38.3.8", {"start": v(-70.03, -21.75) * mm, "end": v(-100.1, -31.09) * mm});
            skArc(sketch, "E38.3.9", {"start": v(-103.49, -16.61) * mm, "mid": v(-102.05, -23.91) * mm, "end": v(-100.1, -31.09) * mm});
            skArc(sketch, "E38.3.10", {"start": v(-82.57, -64.55) * mm, "mid": v(-77.79, -70.25) * mm, "end": v(-72.61, -75.59) * mm});
            skLineSegment(sketch, "E38.3.11", {"start": v(-58.93, -43.63) * mm, "end": v(-84.23, -62.37) * mm});
            skLineSegment(sketch, "E38.3.12", {"start": v(-72.68, -9.72) * mm, "end": v(-103.89, -13.9) * mm});
            skLineSegment(sketch, "E38.3.13", {"start": v(-73.32, 0.65) * mm, "end": v(-104.8, 0.94) * mm});
            skLineSegment(sketch, "E38.3.14", {"start": v(-57.77, -45.16) * mm, "end": v(-82.57, -64.55) * mm});
            skArc(sketch, "E38.3.15", {"start": v(-103.17, 18.46) * mm, "mid": v(-104.22, 11.1) * mm, "end": v(-104.75, 3.68) * mm});
            skLineSegment(sketch, "E38.3.16", {"start": v(-50.8, -52.88) * mm, "end": v(-72.61, -75.59) * mm});
            skArc(sketch, "E38.3.17", {"start": v(-72.4, -11.62) * mm, "mid": v(-71.4, -16.73) * mm, "end": v(-70.03, -21.75) * mm});
            skLineSegment(sketch, "E38.3.18", {"start": v(-72.18, 12.91) * mm, "end": v(-103.17, 18.46) * mm});
            skArc(sketch, "E38.3.19", {"start": v(-99.25, -33.7) * mm, "mid": v(-96.6, -40.65) * mm, "end": v(-93.48, -47.4) * mm});
            skArc(sketch, "E38.3.20", {"start": v(-69.43, -23.57) * mm, "mid": v(-67.59, -28.44) * mm, "end": v(-65.4, -33.16) * mm});
            skLineSegment(sketch, "E38.3.21", {"start": v(-73.28, 2.57) * mm, "end": v(-104.75, 3.68) * mm});
            skLineSegment(sketch, "E38.3.22", {"start": v(-64.5, -34.86) * mm, "end": v(-92.2, -49.83) * mm});
            skArc(sketch, "E38.3.23", {"start": v(-72.18, 12.91) * mm, "mid": v(-72.91, 7.76) * mm, "end": v(-73.28, 2.57) * mm});
            skArc(sketch, "E38.3.24", {"start": v(-73.32, 0.65) * mm, "mid": v(-73.18, -4.55) * mm, "end": v(-72.68, -9.72) * mm});
            skSolve(sketch);
        }
        {
            var Q0;
            Q0=makeQuery(id+"F3.imprint","IMPRINT",FACE,{"disambiguationData":[TD([[makeQuery(id+"F3.imprint","IMPRINT",EDGE,{"derivedFrom":sQuery(id+"F3.wireOp",EDGE,"E38.3.6")}),-1.0]])]});
            var Q1;
            Q1=makeQuery(id+"F3.imprint","IMPRINT",FACE,{"disambiguationData":[TD([[makeQuery(id+"F3.imprint","IMPRINT",EDGE,{"derivedFrom":sQuery(id+"F3.wireOp",EDGE,"E38.3.1")}),-1.0]])]});
            var Q2;
            Q2=makeQuery(id+"F3.imprint","IMPRINT",FACE,{"disambiguationData":[TD([[makeQuery(id+"F3.imprint","IMPRINT",EDGE,{"derivedFrom":sQuery(id+"F3.wireOp",EDGE,"E38.3.5")}),1.0]])]});
            var Q3;
            Q3=makeQuery(id+"F3.imprint","IMPRINT",FACE,{"disambiguationData":[TD([[makeQuery(id+"F3.imprint","IMPRINT",EDGE,{"derivedFrom":sQuery(id+"F3.wireOp",EDGE,"E38.3.7")}),1.0]])]});
            var Q4;
            Q4=makeQuery(id+"F3.imprint","IMPRINT",FACE,{"disambiguationData":[TD([[makeQuery(id+"F3.imprint","IMPRINT",EDGE,{"derivedFrom":sQuery(id+"F3.wireOp",EDGE,"E38.3.15")}),1.0]])]});
            var Q5;
            Q5=makeQuery(id+"F3.imprint","IMPRINT",FACE,{"disambiguationData":[TD([[makeQuery(id+"F3.imprint","IMPRINT",EDGE,{"derivedFrom":sQuery(id+"F3.wireOp",EDGE,"E38.2.6")}),-1.0]])]});
            var Q6;
            Q6=makeQuery(id+"F3.imprint","IMPRINT",FACE,{"disambiguationData":[TD([[makeQuery(id+"F3.imprint","IMPRINT",EDGE,{"derivedFrom":sQuery(id+"F3.wireOp",EDGE,"E38.2.1")}),-1.0]])]});
            var Q7;
            Q7=makeQuery(id+"F3.imprint","IMPRINT",FACE,{"disambiguationData":[TD([[makeQuery(id+"F3.imprint","IMPRINT",EDGE,{"derivedFrom":sQuery(id+"F3.wireOp",EDGE,"E38.2.5")}),1.0]])]});
            var Q8;
            Q8=makeQuery(id+"F3.imprint","IMPRINT",FACE,{"disambiguationData":[TD([[makeQuery(id+"F3.imprint","IMPRINT",EDGE,{"derivedFrom":sQuery(id+"F3.wireOp",EDGE,"E38.2.7")}),1.0]])]});
            var Q9;
            Q9=makeQuery(id+"F3.imprint","IMPRINT",FACE,{"disambiguationData":[TD([[makeQuery(id+"F3.imprint","IMPRINT",EDGE,{"derivedFrom":sQuery(id+"F3.wireOp",EDGE,"E38.2.15")}),1.0]])]});
            var Q10;
            Q10=makeQuery(id+"F3.imprint","IMPRINT",FACE,{"disambiguationData":[TD([[makeQuery(id+"F3.imprint","IMPRINT",EDGE,{"derivedFrom":sQuery(id+"F3.wireOp",EDGE,"E38.1.6")}),-1.0]])]});
            var Q11;
            Q11=makeQuery(id+"F3.imprint","IMPRINT",FACE,{"disambiguationData":[TD([[makeQuery(id+"F3.imprint","IMPRINT",EDGE,{"derivedFrom":sQuery(id+"F3.wireOp",EDGE,"E38.1.1")}),-1.0]])]});
            var Q12;
            Q12=makeQuery(id+"F3.imprint","IMPRINT",FACE,{"disambiguationData":[TD([[makeQuery(id+"F3.imprint","IMPRINT",EDGE,{"derivedFrom":sQuery(id+"F3.wireOp",EDGE,"E38.1.5")}),1.0]])]});
            var Q13;
            Q13=makeQuery(id+"F3.imprint","IMPRINT",FACE,{"disambiguationData":[TD([[makeQuery(id+"F3.imprint","IMPRINT",EDGE,{"derivedFrom":sQuery(id+"F3.wireOp",EDGE,"E38.1.7")}),1.0]])]});
            var Q14;
            Q14=makeQuery(id+"F3.imprint","IMPRINT",FACE,{"disambiguationData":[TD([[makeQuery(id+"F3.imprint","IMPRINT",EDGE,{"derivedFrom":sQuery(id+"F3.wireOp",EDGE,"E38.1.15")}),1.0]])]});
            var Q15;
            Q15=makeQuery(id+"F3.imprint","IMPRINT",FACE,{"disambiguationData":[TD([[makeQuery(id+"F3.imprint","IMPRINT",EDGE,{"derivedFrom":sQuery(id+"F3.wireOp",EDGE,"E15")}),-1.0]])]});
            var Q16;
            Q16=makeQuery(id+"F3.imprint","IMPRINT",FACE,{"disambiguationData":[TD([[makeQuery(id+"F3.imprint","IMPRINT",EDGE,{"derivedFrom":sQuery(id+"F3.wireOp",EDGE,"E19")}),-1.0]])]});
            var Q17;
            Q17=makeQuery(id+"F3.imprint","IMPRINT",FACE,{"disambiguationData":[TD([[makeQuery(id+"F3.imprint","IMPRINT",EDGE,{"derivedFrom":sQuery(id+"F3.wireOp",EDGE,"E26")}),-1.0]])]});
            var Q18;
            Q18=makeQuery(id+"F3.imprint","IMPRINT",FACE,{"disambiguationData":[TD([[makeQuery(id+"F3.imprint","IMPRINT",EDGE,{"derivedFrom":sQuery(id+"F3.wireOp",EDGE,"E30")}),-1.0]])]});
            var Q19;
            Q19=makeQuery(id+"F3.imprint","IMPRINT",FACE,{"disambiguationData":[TD([[makeQuery(id+"F3.imprint","IMPRINT",EDGE,{"derivedFrom":sQuery(id+"F3.wireOp",EDGE,"E14")}),1.0]])]});
            extrude(context, id + "F4", {"entities" : qUnion([Q0, Q1, Q2, Q3, Q4, Q5, Q6, Q7, Q8, Q9, Q10, Q11, Q12, Q13, Q14, Q15, Q16, Q17, Q18, Q19]), "operationType" : NewBodyOperationType.REMOVE, "oppositeDirection" : true, "depth" : 4.5 * mm});
        }
        {
            var Q0;
            Q0=makeQuery(id+"F3.imprint","IMPRINT",FACE,{"disambiguationData":[TD([[makeQuery(id+"F3.imprint","IMPRINT",EDGE,{"derivedFrom":sQuery(id+"F3.wireOp",EDGE,"E38.3.0")}),1.0]])]});
            var Q1;
            Q1=makeQuery(id+"F3.imprint","IMPRINT",FACE,{"disambiguationData":[TD([[makeQuery(id+"F3.imprint","IMPRINT",EDGE,{"derivedFrom":sQuery(id+"F3.wireOp",EDGE,"E38.2.0")}),1.0]])]});
            var Q2;
            Q2=makeQuery(id+"F3.imprint","IMPRINT",FACE,{"disambiguationData":[TD([[makeQuery(id+"F3.imprint","IMPRINT",EDGE,{"derivedFrom":sQuery(id+"F3.wireOp",EDGE,"E38.1.0")}),1.0]])]});
            var Q3;
            Q3=makeQuery(id+"F3.imprint","IMPRINT",FACE,{"disambiguationData":[TD([[makeQuery(id+"F3.imprint","IMPRINT",EDGE,{"derivedFrom":sQuery(id+"F3.wireOp",EDGE,"E25")}),1.0]])]});
            extrude(context, id + "F5", {"entities" : qUnion([Q0, Q1, Q2, Q3]), "operationType" : NewBodyOperationType.REMOVE, "oppositeDirection" : true, "depth" : 2.5 * mm});
        }
        {
            var Q0;
            Q0=makeQuery(id+"F4.boolean.opBoolean","COPY",EDGE,{"derivedFrom":makeQuery(id+"F4.opExtrude","SWEPT_EDGE",EDGE,{"disambiguationData":[OSD([sQuery(id+"F3.wireOp",EDGE,"E38.3.10"),sQuery(id+"F3.wireOp",EDGE,"E38.3.16")])]})});
            var Q1;
            Q1=makeQuery(id+"F4.boolean.opBoolean","COPY",EDGE,{"derivedFrom":makeQuery(id+"F4.opExtrude","SWEPT_EDGE",EDGE,{"disambiguationData":[OSD([sQuery(id+"F3.wireOp",EDGE,"E38.3.2"),sQuery(id+"F3.wireOp",EDGE,"E38.3.11")])]})});
            var Q2;
            Q2=makeQuery(id+"F5.boolean.opBoolean","COPY",EDGE,{"derivedFrom":makeQuery(id+"F5.opExtrude","SWEPT_EDGE",EDGE,{"disambiguationData":[OSD([sQuery(id+"F3.wireOp",EDGE,"E38.3.3"),sQuery(id+"F3.wireOp",EDGE,"E38.3.19")])]})});
            var Q3;
            Q3=makeQuery(id+"F4.boolean.opBoolean","COPY",EDGE,{"derivedFrom":makeQuery(id+"F4.opExtrude","SWEPT_EDGE",EDGE,{"disambiguationData":[OSD([sQuery(id+"F3.wireOp",EDGE,"E38.3.8"),sQuery(id+"F3.wireOp",EDGE,"E38.3.9")])]})});
            var Q4;
            Q4=makeQuery(id+"F4.boolean.opBoolean","COPY",EDGE,{"derivedFrom":makeQuery(id+"F4.opExtrude","SWEPT_EDGE",EDGE,{"disambiguationData":[OSD([sQuery(id+"F3.wireOp",EDGE,"E38.3.7"),sQuery(id+"F3.wireOp",EDGE,"E38.3.12")])]})});
            var Q5;
            Q5=makeQuery(id+"F4.boolean.opBoolean","COPY",EDGE,{"derivedFrom":makeQuery(id+"F4.opExtrude","SWEPT_EDGE",EDGE,{"disambiguationData":[OSD([sQuery(id+"F3.wireOp",EDGE,"E38.3.15"),sQuery(id+"F3.wireOp",EDGE,"E38.3.21")])]})});
            var Q6;
            Q6=makeQuery(id+"F4.boolean.opBoolean","COPY",EDGE,{"derivedFrom":makeQuery(id+"F4.opExtrude","SWEPT_EDGE",EDGE,{"disambiguationData":[OSD([sQuery(id+"F3.wireOp",EDGE,"E38.3.15"),sQuery(id+"F3.wireOp",EDGE,"E38.3.18")])]})});
            var Q7;
            Q7=makeQuery(id+"F4.boolean.opBoolean","COPY",EDGE,{"derivedFrom":makeQuery(id+"F4.opExtrude","SWEPT_EDGE",EDGE,{"disambiguationData":[OSD([sQuery(id+"F3.wireOp",EDGE,"E38.3.7"),sQuery(id+"F3.wireOp",EDGE,"E38.3.13")])]})});
            var Q8;
            Q8=makeQuery(id+"F4.boolean.opBoolean","COPY",EDGE,{"derivedFrom":makeQuery(id+"F4.opExtrude","SWEPT_EDGE",EDGE,{"disambiguationData":[OSD([sQuery(id+"F3.wireOp",EDGE,"E38.3.5"),sQuery(id+"F3.wireOp",EDGE,"E38.3.9")])]})});
            var Q9;
            Q9=makeQuery(id+"F5.boolean.opBoolean","COPY",EDGE,{"derivedFrom":makeQuery(id+"F5.opExtrude","SWEPT_EDGE",EDGE,{"disambiguationData":[OSD([sQuery(id+"F3.wireOp",EDGE,"E38.3.0"),sQuery(id+"F3.wireOp",EDGE,"E38.3.19")])]})});
            var Q10;
            Q10=makeQuery(id+"F4.boolean.opBoolean","COPY",EDGE,{"derivedFrom":makeQuery(id+"F4.opExtrude","SWEPT_EDGE",EDGE,{"disambiguationData":[OSD([sQuery(id+"F3.wireOp",EDGE,"E38.3.2"),sQuery(id+"F3.wireOp",EDGE,"E38.3.22")])]})});
            var Q11;
            Q11=makeQuery(id+"F4.boolean.opBoolean","COPY",EDGE,{"derivedFrom":makeQuery(id+"F4.opExtrude","SWEPT_EDGE",EDGE,{"disambiguationData":[OSD([sQuery(id+"F3.wireOp",EDGE,"E38.3.10"),sQuery(id+"F3.wireOp",EDGE,"E38.3.14")])]})});
            var Q12;
            Q12=makeQuery(id+"F4.boolean.opBoolean","COPY",EDGE,{"derivedFrom":makeQuery(id+"F4.opExtrude","SWEPT_EDGE",EDGE,{"disambiguationData":[OSD([sQuery(id+"F3.wireOp",EDGE,"E38.3.18"),sQuery(id+"F3.wireOp",EDGE,"E38.3.23")])]})});
            var Q13;
            Q13=makeQuery(id+"F4.boolean.opBoolean","COPY",EDGE,{"derivedFrom":makeQuery(id+"F4.opExtrude","SWEPT_EDGE",EDGE,{"disambiguationData":[OSD([sQuery(id+"F3.wireOp",EDGE,"E38.3.13"),sQuery(id+"F3.wireOp",EDGE,"E38.3.24")])]})});
            var Q14;
            Q14=makeQuery(id+"F4.boolean.opBoolean","COPY",EDGE,{"derivedFrom":makeQuery(id+"F4.opExtrude","SWEPT_EDGE",EDGE,{"disambiguationData":[OSD([sQuery(id+"F3.wireOp",EDGE,"E38.3.5"),sQuery(id+"F3.wireOp",EDGE,"E38.3.17")])]})});
            var Q15;
            Q15=makeQuery(id+"F5.boolean.opBoolean","COPY",EDGE,{"derivedFrom":makeQuery(id+"F5.opExtrude","SWEPT_EDGE",EDGE,{"disambiguationData":[OSD([sQuery(id+"F3.wireOp",EDGE,"E38.3.0"),sQuery(id+"F3.wireOp",EDGE,"E38.3.20")])]})});
            var Q16;
            Q16=makeQuery(id+"F4.boolean.opBoolean","COPY",EDGE,{"derivedFrom":makeQuery(id+"F4.opExtrude","SWEPT_EDGE",EDGE,{"disambiguationData":[OSD([sQuery(id+"F3.wireOp",EDGE,"E38.3.1"),sQuery(id+"F3.wireOp",EDGE,"E38.3.22")])]})});
            var Q17;
            Q17=makeQuery(id+"F4.boolean.opBoolean","COPY",EDGE,{"derivedFrom":makeQuery(id+"F4.opExtrude","SWEPT_EDGE",EDGE,{"disambiguationData":[OSD([sQuery(id+"F3.wireOp",EDGE,"E38.3.6"),sQuery(id+"F3.wireOp",EDGE,"E38.3.14")])]})});
            var Q18;
            Q18=makeQuery(id+"F4.boolean.opBoolean","COPY",EDGE,{"derivedFrom":makeQuery(id+"F4.opExtrude","SWEPT_EDGE",EDGE,{"disambiguationData":[OSD([sQuery(id+"F3.wireOp",EDGE,"E38.3.6"),sQuery(id+"F3.wireOp",EDGE,"E38.3.16")])]})});
            var Q19;
            Q19=makeQuery(id+"F4.boolean.opBoolean","COPY",EDGE,{"derivedFrom":makeQuery(id+"F4.opExtrude","SWEPT_EDGE",EDGE,{"disambiguationData":[OSD([sQuery(id+"F3.wireOp",EDGE,"E38.3.1"),sQuery(id+"F3.wireOp",EDGE,"E38.3.11")])]})});
            var Q20;
            Q20=makeQuery(id+"F5.boolean.opBoolean","COPY",EDGE,{"derivedFrom":makeQuery(id+"F5.opExtrude","SWEPT_EDGE",EDGE,{"disambiguationData":[OSD([sQuery(id+"F3.wireOp",EDGE,"E38.3.3"),sQuery(id+"F3.wireOp",EDGE,"E38.3.20")])]})});
            var Q21;
            Q21=makeQuery(id+"F4.boolean.opBoolean","COPY",EDGE,{"derivedFrom":makeQuery(id+"F4.opExtrude","SWEPT_EDGE",EDGE,{"disambiguationData":[OSD([sQuery(id+"F3.wireOp",EDGE,"E38.3.8"),sQuery(id+"F3.wireOp",EDGE,"E38.3.17")])]})});
            var Q22;
            Q22=makeQuery(id+"F4.boolean.opBoolean","COPY",EDGE,{"derivedFrom":makeQuery(id+"F4.opExtrude","SWEPT_EDGE",EDGE,{"disambiguationData":[OSD([sQuery(id+"F3.wireOp",EDGE,"E38.3.12"),sQuery(id+"F3.wireOp",EDGE,"E38.3.24")])]})});
            var Q23;
            Q23=makeQuery(id+"F4.boolean.opBoolean","COPY",EDGE,{"derivedFrom":makeQuery(id+"F4.opExtrude","SWEPT_EDGE",EDGE,{"disambiguationData":[OSD([sQuery(id+"F3.wireOp",EDGE,"E38.3.21"),sQuery(id+"F3.wireOp",EDGE,"E38.3.23")])]})});
            var Q24;
            Q24=makeQuery(id+"F4.boolean.opBoolean","COPY",EDGE,{"derivedFrom":makeQuery(id+"F4.opExtrude","SWEPT_EDGE",EDGE,{"disambiguationData":[OSD([sQuery(id+"F3.wireOp",EDGE,"E38.2.6"),sQuery(id+"F3.wireOp",EDGE,"E38.2.16")])]})});
            var Q25;
            Q25=makeQuery(id+"F4.boolean.opBoolean","COPY",EDGE,{"derivedFrom":makeQuery(id+"F4.opExtrude","SWEPT_EDGE",EDGE,{"disambiguationData":[OSD([sQuery(id+"F3.wireOp",EDGE,"E38.2.1"),sQuery(id+"F3.wireOp",EDGE,"E38.2.11")])]})});
            var Q26;
            Q26=makeQuery(id+"F5.boolean.opBoolean","COPY",EDGE,{"derivedFrom":makeQuery(id+"F5.opExtrude","SWEPT_EDGE",EDGE,{"disambiguationData":[OSD([sQuery(id+"F3.wireOp",EDGE,"E38.2.3"),sQuery(id+"F3.wireOp",EDGE,"E38.2.20")])]})});
            var Q27;
            Q27=makeQuery(id+"F4.boolean.opBoolean","COPY",EDGE,{"derivedFrom":makeQuery(id+"F4.opExtrude","SWEPT_EDGE",EDGE,{"disambiguationData":[OSD([sQuery(id+"F3.wireOp",EDGE,"E38.2.8"),sQuery(id+"F3.wireOp",EDGE,"E38.2.17")])]})});
            var Q28;
            Q28=makeQuery(id+"F4.boolean.opBoolean","COPY",EDGE,{"derivedFrom":makeQuery(id+"F4.opExtrude","SWEPT_EDGE",EDGE,{"disambiguationData":[OSD([sQuery(id+"F3.wireOp",EDGE,"E38.2.12"),sQuery(id+"F3.wireOp",EDGE,"E38.2.24")])]})});
            var Q29;
            Q29=makeQuery(id+"F4.boolean.opBoolean","COPY",EDGE,{"derivedFrom":makeQuery(id+"F4.opExtrude","SWEPT_EDGE",EDGE,{"disambiguationData":[OSD([sQuery(id+"F3.wireOp",EDGE,"E38.2.21"),sQuery(id+"F3.wireOp",EDGE,"E38.2.23")])]})});
            var Q30;
            Q30=makeQuery(id+"F4.boolean.opBoolean","COPY",EDGE,{"derivedFrom":makeQuery(id+"F4.opExtrude","SWEPT_EDGE",EDGE,{"disambiguationData":[OSD([sQuery(id+"F3.wireOp",EDGE,"E38.2.18"),sQuery(id+"F3.wireOp",EDGE,"E38.2.23")])]})});
            var Q31;
            Q31=makeQuery(id+"F4.boolean.opBoolean","COPY",EDGE,{"derivedFrom":makeQuery(id+"F4.opExtrude","SWEPT_EDGE",EDGE,{"disambiguationData":[OSD([sQuery(id+"F3.wireOp",EDGE,"E38.2.13"),sQuery(id+"F3.wireOp",EDGE,"E38.2.24")])]})});
            var Q32;
            Q32=makeQuery(id+"F4.boolean.opBoolean","COPY",EDGE,{"derivedFrom":makeQuery(id+"F4.opExtrude","SWEPT_EDGE",EDGE,{"disambiguationData":[OSD([sQuery(id+"F3.wireOp",EDGE,"E38.2.5"),sQuery(id+"F3.wireOp",EDGE,"E38.2.17")])]})});
            var Q33;
            Q33=makeQuery(id+"F5.boolean.opBoolean","COPY",EDGE,{"derivedFrom":makeQuery(id+"F5.opExtrude","SWEPT_EDGE",EDGE,{"disambiguationData":[OSD([sQuery(id+"F3.wireOp",EDGE,"E38.2.0"),sQuery(id+"F3.wireOp",EDGE,"E38.2.20")])]})});
            var Q34;
            Q34=makeQuery(id+"F4.boolean.opBoolean","COPY",EDGE,{"derivedFrom":makeQuery(id+"F4.opExtrude","SWEPT_EDGE",EDGE,{"disambiguationData":[OSD([sQuery(id+"F3.wireOp",EDGE,"E38.2.1"),sQuery(id+"F3.wireOp",EDGE,"E38.2.22")])]})});
            var Q35;
            Q35=makeQuery(id+"F4.boolean.opBoolean","COPY",EDGE,{"derivedFrom":makeQuery(id+"F4.opExtrude","SWEPT_EDGE",EDGE,{"disambiguationData":[OSD([sQuery(id+"F3.wireOp",EDGE,"E38.2.6"),sQuery(id+"F3.wireOp",EDGE,"E38.2.14")])]})});
            var Q36;
            Q36=makeQuery(id+"F4.boolean.opBoolean","COPY",EDGE,{"derivedFrom":makeQuery(id+"F4.opExtrude","SWEPT_EDGE",EDGE,{"disambiguationData":[OSD([sQuery(id+"F3.wireOp",EDGE,"E38.2.10"),sQuery(id+"F3.wireOp",EDGE,"E38.2.16")])]})});
            var Q37;
            Q37=makeQuery(id+"F4.boolean.opBoolean","COPY",EDGE,{"derivedFrom":makeQuery(id+"F4.opExtrude","SWEPT_EDGE",EDGE,{"disambiguationData":[OSD([sQuery(id+"F3.wireOp",EDGE,"E38.2.2"),sQuery(id+"F3.wireOp",EDGE,"E38.2.11")])]})});
            var Q38;
            Q38=makeQuery(id+"F5.boolean.opBoolean","COPY",EDGE,{"derivedFrom":makeQuery(id+"F5.opExtrude","SWEPT_EDGE",EDGE,{"disambiguationData":[OSD([sQuery(id+"F3.wireOp",EDGE,"E38.2.3"),sQuery(id+"F3.wireOp",EDGE,"E38.2.19")])]})});
            var Q39;
            Q39=makeQuery(id+"F4.boolean.opBoolean","COPY",EDGE,{"derivedFrom":makeQuery(id+"F4.opExtrude","SWEPT_EDGE",EDGE,{"disambiguationData":[OSD([sQuery(id+"F3.wireOp",EDGE,"E38.2.8"),sQuery(id+"F3.wireOp",EDGE,"E38.2.9")])]})});
            var Q40;
            Q40=makeQuery(id+"F4.boolean.opBoolean","COPY",EDGE,{"derivedFrom":makeQuery(id+"F4.opExtrude","SWEPT_EDGE",EDGE,{"disambiguationData":[OSD([sQuery(id+"F3.wireOp",EDGE,"E38.2.7"),sQuery(id+"F3.wireOp",EDGE,"E38.2.12")])]})});
            var Q41;
            Q41=makeQuery(id+"F4.boolean.opBoolean","COPY",EDGE,{"derivedFrom":makeQuery(id+"F4.opExtrude","SWEPT_EDGE",EDGE,{"disambiguationData":[OSD([sQuery(id+"F3.wireOp",EDGE,"E38.2.15"),sQuery(id+"F3.wireOp",EDGE,"E38.2.21")])]})});
            var Q42;
            Q42=makeQuery(id+"F4.boolean.opBoolean","COPY",EDGE,{"derivedFrom":makeQuery(id+"F4.opExtrude","SWEPT_EDGE",EDGE,{"disambiguationData":[OSD([sQuery(id+"F3.wireOp",EDGE,"E38.2.5"),sQuery(id+"F3.wireOp",EDGE,"E38.2.9")])]})});
            var Q43;
            Q43=makeQuery(id+"F5.boolean.opBoolean","COPY",EDGE,{"derivedFrom":makeQuery(id+"F5.opExtrude","SWEPT_EDGE",EDGE,{"disambiguationData":[OSD([sQuery(id+"F3.wireOp",EDGE,"E38.2.0"),sQuery(id+"F3.wireOp",EDGE,"E38.2.19")])]})});
            var Q44;
            Q44=makeQuery(id+"F4.boolean.opBoolean","COPY",EDGE,{"derivedFrom":makeQuery(id+"F4.opExtrude","SWEPT_EDGE",EDGE,{"disambiguationData":[OSD([sQuery(id+"F3.wireOp",EDGE,"E38.2.2"),sQuery(id+"F3.wireOp",EDGE,"E38.2.22")])]})});
            var Q45;
            Q45=makeQuery(id+"F4.boolean.opBoolean","COPY",EDGE,{"derivedFrom":makeQuery(id+"F4.opExtrude","SWEPT_EDGE",EDGE,{"disambiguationData":[OSD([sQuery(id+"F3.wireOp",EDGE,"E38.2.10"),sQuery(id+"F3.wireOp",EDGE,"E38.2.14")])]})});
            var Q46;
            Q46=makeQuery(id+"F4.boolean.opBoolean","COPY",EDGE,{"derivedFrom":makeQuery(id+"F4.opExtrude","SWEPT_EDGE",EDGE,{"disambiguationData":[OSD([sQuery(id+"F3.wireOp",EDGE,"E38.2.7"),sQuery(id+"F3.wireOp",EDGE,"E38.2.13")])]})});
            var Q47;
            Q47=makeQuery(id+"F4.boolean.opBoolean","COPY",EDGE,{"derivedFrom":makeQuery(id+"F4.opExtrude","SWEPT_EDGE",EDGE,{"disambiguationData":[OSD([sQuery(id+"F3.wireOp",EDGE,"E38.2.15"),sQuery(id+"F3.wireOp",EDGE,"E38.2.18")])]})});
            var Q48;
            Q48=makeQuery(id+"F4.boolean.opBoolean","COPY",EDGE,{"derivedFrom":makeQuery(id+"F4.opExtrude","SWEPT_EDGE",EDGE,{"disambiguationData":[OSD([sQuery(id+"F3.wireOp",EDGE,"E38.1.10"),sQuery(id+"F3.wireOp",EDGE,"E38.1.14")])]})});
            var Q49;
            Q49=makeQuery(id+"F4.boolean.opBoolean","COPY",EDGE,{"derivedFrom":makeQuery(id+"F4.opExtrude","SWEPT_EDGE",EDGE,{"disambiguationData":[OSD([sQuery(id+"F3.wireOp",EDGE,"E38.1.2"),sQuery(id+"F3.wireOp",EDGE,"E38.1.22")])]})});
            var Q50;
            Q50=makeQuery(id+"F5.boolean.opBoolean","COPY",EDGE,{"derivedFrom":makeQuery(id+"F5.opExtrude","SWEPT_EDGE",EDGE,{"disambiguationData":[OSD([sQuery(id+"F3.wireOp",EDGE,"E38.1.0"),sQuery(id+"F3.wireOp",EDGE,"E38.1.19")])]})});
            var Q51;
            Q51=makeQuery(id+"F4.boolean.opBoolean","COPY",EDGE,{"derivedFrom":makeQuery(id+"F4.opExtrude","SWEPT_EDGE",EDGE,{"disambiguationData":[OSD([sQuery(id+"F3.wireOp",EDGE,"E38.1.5"),sQuery(id+"F3.wireOp",EDGE,"E38.1.9")])]})});
            var Q52;
            Q52=makeQuery(id+"F4.boolean.opBoolean","COPY",EDGE,{"derivedFrom":makeQuery(id+"F4.opExtrude","SWEPT_EDGE",EDGE,{"disambiguationData":[OSD([sQuery(id+"F3.wireOp",EDGE,"E38.1.7"),sQuery(id+"F3.wireOp",EDGE,"E38.1.13")])]})});
            var Q53;
            Q53=makeQuery(id+"F4.boolean.opBoolean","COPY",EDGE,{"derivedFrom":makeQuery(id+"F4.opExtrude","SWEPT_EDGE",EDGE,{"disambiguationData":[OSD([sQuery(id+"F3.wireOp",EDGE,"E38.1.15"),sQuery(id+"F3.wireOp",EDGE,"E38.1.18")])]})});
            var Q54;
            Q54=makeQuery(id+"F4.boolean.opBoolean","COPY",EDGE,{"derivedFrom":makeQuery(id+"F4.opExtrude","SWEPT_EDGE",EDGE,{"disambiguationData":[OSD([sQuery(id+"F3.wireOp",EDGE,"E38.1.15"),sQuery(id+"F3.wireOp",EDGE,"E38.1.21")])]})});
            var Q55;
            Q55=makeQuery(id+"F4.boolean.opBoolean","COPY",EDGE,{"derivedFrom":makeQuery(id+"F4.opExtrude","SWEPT_EDGE",EDGE,{"disambiguationData":[OSD([sQuery(id+"F3.wireOp",EDGE,"E38.1.7"),sQuery(id+"F3.wireOp",EDGE,"E38.1.12")])]})});
            var Q56;
            Q56=makeQuery(id+"F4.boolean.opBoolean","COPY",EDGE,{"derivedFrom":makeQuery(id+"F4.opExtrude","SWEPT_EDGE",EDGE,{"disambiguationData":[OSD([sQuery(id+"F3.wireOp",EDGE,"E38.1.8"),sQuery(id+"F3.wireOp",EDGE,"E38.1.9")])]})});
            var Q57;
            Q57=makeQuery(id+"F5.boolean.opBoolean","COPY",EDGE,{"derivedFrom":makeQuery(id+"F5.opExtrude","SWEPT_EDGE",EDGE,{"disambiguationData":[OSD([sQuery(id+"F3.wireOp",EDGE,"E38.1.3"),sQuery(id+"F3.wireOp",EDGE,"E38.1.19")])]})});
            var Q58;
            Q58=makeQuery(id+"F4.boolean.opBoolean","COPY",EDGE,{"derivedFrom":makeQuery(id+"F4.opExtrude","SWEPT_EDGE",EDGE,{"disambiguationData":[OSD([sQuery(id+"F3.wireOp",EDGE,"E38.1.2"),sQuery(id+"F3.wireOp",EDGE,"E38.1.11")])]})});
            var Q59;
            Q59=makeQuery(id+"F4.boolean.opBoolean","COPY",EDGE,{"derivedFrom":makeQuery(id+"F4.opExtrude","SWEPT_EDGE",EDGE,{"disambiguationData":[OSD([sQuery(id+"F3.wireOp",EDGE,"E38.1.10"),sQuery(id+"F3.wireOp",EDGE,"E38.1.16")])]})});
            var Q60;
            Q60=makeQuery(id+"F4.boolean.opBoolean","COPY",EDGE,{"derivedFrom":makeQuery(id+"F4.opExtrude","SWEPT_EDGE",EDGE,{"disambiguationData":[OSD([sQuery(id+"F3.wireOp",EDGE,"E38.1.6"),sQuery(id+"F3.wireOp",EDGE,"E38.1.16")])]})});
            var Q61;
            Q61=makeQuery(id+"F4.boolean.opBoolean","COPY",EDGE,{"derivedFrom":makeQuery(id+"F4.opExtrude","SWEPT_EDGE",EDGE,{"disambiguationData":[OSD([sQuery(id+"F3.wireOp",EDGE,"E38.1.1"),sQuery(id+"F3.wireOp",EDGE,"E38.1.11")])]})});
            var Q62;
            Q62=makeQuery(id+"F5.boolean.opBoolean","COPY",EDGE,{"derivedFrom":makeQuery(id+"F5.opExtrude","SWEPT_EDGE",EDGE,{"disambiguationData":[OSD([sQuery(id+"F3.wireOp",EDGE,"E38.1.3"),sQuery(id+"F3.wireOp",EDGE,"E38.1.20")])]})});
            var Q63;
            Q63=makeQuery(id+"F4.boolean.opBoolean","COPY",EDGE,{"derivedFrom":makeQuery(id+"F4.opExtrude","SWEPT_EDGE",EDGE,{"disambiguationData":[OSD([sQuery(id+"F3.wireOp",EDGE,"E38.1.8"),sQuery(id+"F3.wireOp",EDGE,"E38.1.17")])]})});
            var Q64;
            Q64=makeQuery(id+"F4.boolean.opBoolean","COPY",EDGE,{"derivedFrom":makeQuery(id+"F4.opExtrude","SWEPT_EDGE",EDGE,{"disambiguationData":[OSD([sQuery(id+"F3.wireOp",EDGE,"E38.1.12"),sQuery(id+"F3.wireOp",EDGE,"E38.1.24")])]})});
            var Q65;
            Q65=makeQuery(id+"F4.boolean.opBoolean","COPY",EDGE,{"derivedFrom":makeQuery(id+"F4.opExtrude","SWEPT_EDGE",EDGE,{"disambiguationData":[OSD([sQuery(id+"F3.wireOp",EDGE,"E38.1.21"),sQuery(id+"F3.wireOp",EDGE,"E38.1.23")])]})});
            var Q66;
            Q66=makeQuery(id+"F4.boolean.opBoolean","COPY",EDGE,{"derivedFrom":makeQuery(id+"F4.opExtrude","SWEPT_EDGE",EDGE,{"disambiguationData":[OSD([sQuery(id+"F3.wireOp",EDGE,"E38.1.6"),sQuery(id+"F3.wireOp",EDGE,"E38.1.14")])]})});
            var Q67;
            Q67=makeQuery(id+"F4.boolean.opBoolean","COPY",EDGE,{"derivedFrom":makeQuery(id+"F4.opExtrude","SWEPT_EDGE",EDGE,{"disambiguationData":[OSD([sQuery(id+"F3.wireOp",EDGE,"E38.1.1"),sQuery(id+"F3.wireOp",EDGE,"E38.1.22")])]})});
            var Q68;
            Q68=makeQuery(id+"F5.boolean.opBoolean","COPY",EDGE,{"derivedFrom":makeQuery(id+"F5.opExtrude","SWEPT_EDGE",EDGE,{"disambiguationData":[OSD([sQuery(id+"F3.wireOp",EDGE,"E38.1.0"),sQuery(id+"F3.wireOp",EDGE,"E38.1.20")])]})});
            var Q69;
            Q69=makeQuery(id+"F4.boolean.opBoolean","COPY",EDGE,{"derivedFrom":makeQuery(id+"F4.opExtrude","SWEPT_EDGE",EDGE,{"disambiguationData":[OSD([sQuery(id+"F3.wireOp",EDGE,"E38.1.5"),sQuery(id+"F3.wireOp",EDGE,"E38.1.17")])]})});
            var Q70;
            Q70=makeQuery(id+"F4.boolean.opBoolean","COPY",EDGE,{"derivedFrom":makeQuery(id+"F4.opExtrude","SWEPT_EDGE",EDGE,{"disambiguationData":[OSD([sQuery(id+"F3.wireOp",EDGE,"E38.1.18"),sQuery(id+"F3.wireOp",EDGE,"E38.1.23")])]})});
            var Q71;
            Q71=makeQuery(id+"F4.boolean.opBoolean","COPY",EDGE,{"derivedFrom":makeQuery(id+"F4.opExtrude","SWEPT_EDGE",EDGE,{"disambiguationData":[OSD([sQuery(id+"F3.wireOp",EDGE,"E15"),sQuery(id+"F3.wireOp",EDGE,"E21.trimOffspring")])]})});
            var Q72;
            Q72=makeQuery(id+"F4.boolean.opBoolean","COPY",EDGE,{"derivedFrom":makeQuery(id+"F4.opExtrude","SWEPT_EDGE",EDGE,{"disambiguationData":[OSD([sQuery(id+"F3.wireOp",EDGE,"E19"),sQuery(id+"F3.wireOp",EDGE,"E23.trimOffspring")])]})});
            var Q73;
            Q73=makeQuery(id+"F5.boolean.opBoolean","COPY",EDGE,{"derivedFrom":makeQuery(id+"F5.opExtrude","SWEPT_EDGE",EDGE,{"disambiguationData":[OSD([sQuery(id+"F3.wireOp",EDGE,"E27.trimOffspring"),sQuery(id+"F3.wireOp",EDGE,"E37")])]})});
            var Q74;
            Q74=makeQuery(id+"F4.boolean.opBoolean","COPY",EDGE,{"derivedFrom":makeQuery(id+"F4.opExtrude","SWEPT_EDGE",EDGE,{"disambiguationData":[OSD([sQuery(id+"F3.wireOp",EDGE,"E26"),sQuery(id+"F3.wireOp",EDGE,"E31.trimOffspring")])]})});
            var Q75;
            Q75=makeQuery(id+"F4.boolean.opBoolean","COPY",EDGE,{"derivedFrom":makeQuery(id+"F4.opExtrude","SWEPT_EDGE",EDGE,{"disambiguationData":[OSD([sQuery(id+"F3.wireOp",EDGE,"E30"),sQuery(id+"F3.wireOp",EDGE,"E35.trimOffspring")])]})});
            var Q76;
            Q76=makeQuery(id+"F4.boolean.opBoolean","COPY",EDGE,{"derivedFrom":makeQuery(id+"F4.opExtrude","SWEPT_EDGE",EDGE,{"disambiguationData":[OSD([sQuery(id+"F3.wireOp",EDGE,"E17"),sQuery(id+"F3.wireOp",EDGE,"E34")])]})});
            var Q77;
            Q77=makeQuery(id+"F4.boolean.opBoolean","COPY",EDGE,{"derivedFrom":makeQuery(id+"F4.opExtrude","SWEPT_EDGE",EDGE,{"disambiguationData":[OSD([sQuery(id+"F3.wireOp",EDGE,"E18"),sQuery(id+"F3.wireOp",EDGE,"E21.trimOffspring")])]})});
            var Q78;
            Q78=makeQuery(id+"F4.boolean.opBoolean","COPY",EDGE,{"derivedFrom":makeQuery(id+"F4.opExtrude","SWEPT_EDGE",EDGE,{"disambiguationData":[OSD([sQuery(id+"F3.wireOp",EDGE,"E22"),sQuery(id+"F3.wireOp",EDGE,"E23.trimOffspring")])]})});
            var Q79;
            Q79=makeQuery(id+"F5.boolean.opBoolean","COPY",EDGE,{"derivedFrom":makeQuery(id+"F5.opExtrude","SWEPT_EDGE",EDGE,{"disambiguationData":[OSD([sQuery(id+"F3.wireOp",EDGE,"E25"),sQuery(id+"F3.wireOp",EDGE,"E27.trimOffspring")])]})});
            var Q80;
            Q80=makeQuery(id+"F4.boolean.opBoolean","COPY",EDGE,{"derivedFrom":makeQuery(id+"F4.opExtrude","SWEPT_EDGE",EDGE,{"disambiguationData":[OSD([sQuery(id+"F3.wireOp",EDGE,"E29"),sQuery(id+"F3.wireOp",EDGE,"E31.trimOffspring")])]})});
            var Q81;
            Q81=makeQuery(id+"F4.boolean.opBoolean","COPY",EDGE,{"derivedFrom":makeQuery(id+"F4.opExtrude","SWEPT_EDGE",EDGE,{"disambiguationData":[OSD([sQuery(id+"F3.wireOp",EDGE,"E33"),sQuery(id+"F3.wireOp",EDGE,"E35.trimOffspring")])]})});
            var Q82;
            Q82=makeQuery(id+"F4.boolean.opBoolean","COPY",EDGE,{"derivedFrom":makeQuery(id+"F4.opExtrude","SWEPT_EDGE",EDGE,{"disambiguationData":[OSD([sQuery(id+"F3.wireOp",EDGE,"E14"),sQuery(id+"F3.wireOp",EDGE,"E17")])]})});
            var Q83;
            Q83=makeQuery(id+"F4.boolean.opBoolean","COPY",EDGE,{"derivedFrom":makeQuery(id+"F4.opExtrude","SWEPT_EDGE",EDGE,{"disambiguationData":[OSD([sQuery(id+"F3.wireOp",EDGE,"E15"),sQuery(id+"F3.wireOp",EDGE,"E20.trimOffspring")])]})});
            var Q84;
            Q84=makeQuery(id+"F4.boolean.opBoolean","COPY",EDGE,{"derivedFrom":makeQuery(id+"F4.opExtrude","SWEPT_EDGE",EDGE,{"disambiguationData":[OSD([sQuery(id+"F3.wireOp",EDGE,"E19"),sQuery(id+"F3.wireOp",EDGE,"E24.trimOffspring")])]})});
            var Q85;
            Q85=makeQuery(id+"F5.boolean.opBoolean","COPY",EDGE,{"derivedFrom":makeQuery(id+"F5.opExtrude","SWEPT_EDGE",EDGE,{"disambiguationData":[OSD([sQuery(id+"F3.wireOp",EDGE,"E28.trimOffspring"),sQuery(id+"F3.wireOp",EDGE,"E37")])]})});
            var Q86;
            Q86=makeQuery(id+"F4.boolean.opBoolean","COPY",EDGE,{"derivedFrom":makeQuery(id+"F4.opExtrude","SWEPT_EDGE",EDGE,{"disambiguationData":[OSD([sQuery(id+"F3.wireOp",EDGE,"E30"),sQuery(id+"F3.wireOp",EDGE,"E36.trimOffspring")])]})});
            var Q87;
            Q87=makeQuery(id+"F4.boolean.opBoolean","COPY",EDGE,{"derivedFrom":makeQuery(id+"F4.opExtrude","SWEPT_EDGE",EDGE,{"disambiguationData":[OSD([sQuery(id+"F3.wireOp",EDGE,"E16"),sQuery(id+"F3.wireOp",EDGE,"E34")])]})});
            var Q88;
            Q88=makeQuery(id+"F4.boolean.opBoolean","COPY",EDGE,{"derivedFrom":makeQuery(id+"F4.opExtrude","SWEPT_EDGE",EDGE,{"disambiguationData":[OSD([sQuery(id+"F3.wireOp",EDGE,"E18"),sQuery(id+"F3.wireOp",EDGE,"E20.trimOffspring")])]})});
            var Q89;
            Q89=makeQuery(id+"F4.boolean.opBoolean","COPY",EDGE,{"derivedFrom":makeQuery(id+"F4.opExtrude","SWEPT_EDGE",EDGE,{"disambiguationData":[OSD([sQuery(id+"F3.wireOp",EDGE,"E22"),sQuery(id+"F3.wireOp",EDGE,"E24.trimOffspring")])]})});
            var Q90;
            Q90=makeQuery(id+"F5.boolean.opBoolean","COPY",EDGE,{"derivedFrom":makeQuery(id+"F5.opExtrude","SWEPT_EDGE",EDGE,{"disambiguationData":[OSD([sQuery(id+"F3.wireOp",EDGE,"E25"),sQuery(id+"F3.wireOp",EDGE,"E28.trimOffspring")])]})});
            var Q91;
            Q91=makeQuery(id+"F4.boolean.opBoolean","COPY",EDGE,{"derivedFrom":makeQuery(id+"F4.opExtrude","SWEPT_EDGE",EDGE,{"disambiguationData":[OSD([sQuery(id+"F3.wireOp",EDGE,"E29"),sQuery(id+"F3.wireOp",EDGE,"E32.trimOffspring")])]})});
            var Q92;
            Q92=makeQuery(id+"F4.boolean.opBoolean","COPY",EDGE,{"derivedFrom":makeQuery(id+"F4.opExtrude","SWEPT_EDGE",EDGE,{"disambiguationData":[OSD([sQuery(id+"F3.wireOp",EDGE,"E33"),sQuery(id+"F3.wireOp",EDGE,"E36.trimOffspring")])]})});
            var Q93;
            Q93=makeQuery(id+"F4.boolean.opBoolean","COPY",EDGE,{"derivedFrom":makeQuery(id+"F4.opExtrude","SWEPT_EDGE",EDGE,{"disambiguationData":[OSD([sQuery(id+"F3.wireOp",EDGE,"E14"),sQuery(id+"F3.wireOp",EDGE,"E16")])]})});
            fillet(context, id + "F6", {"entities" : qUnion([Q0, Q1, Q2, Q3, Q4, Q5, Q6, Q7, Q8, Q9, Q10, Q11, Q12, Q13, Q14, Q15, Q16, Q17, Q18, Q19, Q20, Q21, Q22, Q23, Q24, Q25, Q26, Q27, Q28, Q29, Q30, Q31, Q32, Q33, Q34, Q35, Q36, Q37, Q38, Q39, Q40, Q41, Q42, Q43, Q44, Q45, Q46, Q47, Q48, Q49, Q50, Q51, Q52, Q53, Q54, Q55, Q56, Q57, Q58, Q59, Q60, Q61, Q62, Q63, Q64, Q65, Q66, Q67, Q68, Q69, Q70, Q71, Q72, Q73, Q74, Q75, Q76, Q77, Q78, Q79, Q80, Q81, Q82, Q83, Q84, Q85, Q86, Q87, Q88, Q89, Q90, Q91, Q92, Q93]), "radius" : 2 * mm, "tangentPropagation" : true, "allowEdgeOverflow" : false});
        }
    });
